FCSTD DOCUMENT  (FreeCAD 1.0R39319 (Git))
Label: Assembly
License: All rights reserved
LicenseURL: https://en.wikipedia.org/wiki/All_rights_reserved
objects: App::Link×10, App::FeaturePython×9, Assembly::JointGroup×1, Assembly::AssemblyObject×1
EXTERNAL_REF file=TopEnclosureShell.FCStd obj=Body002
EXTERNAL_REF file=Spec.FCStd obj=Spreadsheet
EXTERNAL_REF file=TopEnclosureDisplayFront.FCStd obj=Body
EXTERNAL_REF file=TopEnclosureDisplayBack.FCStd obj=Body
EXTERNAL_REF file=TopEnclosureBack_v2.FCStd obj=Body
EXTERNAL_REF file=BottomEnclosure_base_split.FCStd obj=Body002
EXTERNAL_REF file=BottomEnclosure_base_split.FCStd obj=Body003
EXTERNAL_REF file=TopEnclosureHood_v2.FCStd obj=Body
EXTERNAL_REF file=CM5-IO-BASE-B.FCStd obj=PCB

FEATURE [App::Link] Link  label="Top Enclosure Shell - 2"
  LinkPlacement = pos=(-0.4,61.7894,81.5417) rot=(1,0,0;1.0472rad)
  LinkedObject = -> <external TopEnclosureShell.FCStd>#Body002
  Placement = pos=(-0.4,61.7894,81.5417) rot=(1,0,0;1.0472rad)
FEATURE [App::Link] Link002  label="Vars"
  LinkedObject = -> <external Spec.FCStd>#Spreadsheet
FEATURE [App::Link] Top_Enclosure_Display_Front  label="Top Enclosure Display Front"
  LinkPlacement = pos=(-0.4,53.3024,86.4417) rot=(1,0,0;1.0472rad)
  LinkedObject = -> <external TopEnclosureDisplayFront.FCStd>#Body
  Placement = pos=(-0.4,53.3024,86.4417) rot=(1,0,0;1.0472rad)
FEATURE [App::Link] Top_Enclosure_Display_Back  label="Top Enclosure Display Back"
  LinkPlacement = pos=(-0.4,54.6014,85.6917) rot=(0,-0.5,0.866025;3.14159rad)
  LinkedObject = -> <external TopEnclosureDisplayBack.FCStd>#Body
  Placement = pos=(-0.4,54.6014,85.6917) rot=(0,-0.5,0.866025;3.14159rad)
FEATURE [App::Link] Top_Enclosure_Back  label="Top Enclosure Back"
  LinkPlacement = pos=(-0.4,59.4512,82.8917) rot=(0,0.866025,0.5;3.14159rad)
  LinkedObject = -> <external TopEnclosureBack_v2.FCStd>#Body
  Placement = pos=(-0.4,59.4512,82.8917) rot=(0,0.866025,0.5;3.14159rad)
FEATURE [App::Link] Bottom_Enclosure___Bottom  label="Bottom Enclosure - Bottom"
  LinkedObject = -> <external BottomEnclosure_base_split.FCStd>#Body002
FEATURE [App::FeaturePython] GroundedJoint001  # Assembly grounded joint (typed FeaturePython)
  ObjectToGround = -> Bottom_Enclosure___Bottom
FEATURE [App::Link] Bottom_Enclosure___Top  label="Bottom Enclosure - Top"
  LinkPlacement = pos=(1.05e-14,-1.7e-15,5e-16) rot=(0,0,1;0rad)
  LinkedObject = -> <external BottomEnclosure_base_split.FCStd>#Body003
  Placement = pos=(1.05e-14,-1.7e-15,5e-16) rot=(0,0,1;0rad)
FEATURE [App::Link] Top_Enclosure_Hood  label="Top Enclosure Hood"
  LinkPlacement = pos=(-0.4,50.0115,88.3417) rot=(1,0,0;1.0472rad)
  LinkedObject = -> <external TopEnclosureHood_v2.FCStd>#Body
  Placement = pos=(-0.4,50.0115,88.3417) rot=(1,0,0;1.0472rad)
FEATURE [App::Link] PCB
  LinkPlacement = pos=(-110,162,8.00005) rot=(0,0,1;0rad)
  LinkedObject = -> <external CM5-IO-BASE-B.FCStd>#PCB
  Placement = pos=(-110,162,8.00005) rot=(0,0,1;0rad)
FEATURE [App::FeaturePython] Joint  label="Fixed"  # Assembly joint (typed FeaturePython)
  Activated = true
  AngleMax = 0
  AngleMin = 0
  Detach1 = false
  Detach2 = false
  Distance = 0
  Distance2 = 0
  EnableAngleMax = false
  EnableAngleMin = false
  EnableLengthMax = false
  EnableLengthMin = false
  JointType = 0 (Fixed)
  LengthMax = 0
  LengthMin = 0
  Placement1 = pos=(-130,50,15) rot=(1,0,0;3.14159rad)
  Placement2 = pos=(-130,50,15) rot=(1,0,0;3.14159rad)
  Reference1 = -> Assembly [Bottom_Enclosure___Bottom.Edge52,Bottom_Enclosure___Bottom.Edge52]
  Reference2 = -> Assembly [Bottom_Enclosure___Top.Edge108,Bottom_Enclosure___Top.Edge108]
FEATURE [App::FeaturePython] Joint001  label="Cylindrical"  # Assembly joint (typed FeaturePython)
  Activated = true
  AngleMax = 60
  AngleMin = 40
  Detach1 = false
  Detach2 = false
  Distance = 0
  Distance2 = 0
  EnableAngleMax = true
  EnableAngleMin = true
  EnableLengthMax = false
  EnableLengthMin = false
  JointType = 2 (Cylindrical)
  LengthMax = 0
  LengthMin = 0
  Placement1 = pos=(-110.4,15,33.5) rot=(0.57735,0.57735,0.57735;2.0944rad)
  Placement2 = pos=(-108,-65,16.5) rot=(0.57735,0.57735,0.57735;2.0944rad)
  Reference1 = -> Assembly [Bottom_Enclosure___Top.Edge146,Bottom_Enclosure___Top.Edge146]
  Reference2 = -> Assembly [Link.Edge118,Link.Edge118]
FEATURE [App::FeaturePython] Joint002  label="Angle"  # Assembly joint (typed FeaturePython)
  Activated = true
  AngleMax = 0
  AngleMin = 0
  Detach1 = false
  Detach2 = false
  Distance = 0
  Distance2 = 0
  EnableAngleMax = false
  EnableAngleMin = false
  EnableLengthMax = false
  EnableLengthMin = false
  JointType = 8 (Angle)
  LengthMax = 0
  LengthMin = 0
  Placement1 = pos=(117.9,31.739,38.8469) rot=(-0.250563,0.250563,0.935113;1.63783rad)
  Placement2 = pos=(130,-50,-7.1e-15) rot=(-1,0,0;1.5708rad)
  Reference1 = -> Assembly [Bottom_Enclosure___Top.Face63,Bottom_Enclosure___Top.Face63]
  Reference2 = -> Assembly [Link.Face9,Link.Vertex11]
FEATURE [App::FeaturePython] Joint003  label="Distance"  # Assembly joint (typed FeaturePython)
  Activated = true
  AngleMax = 0
  AngleMin = 0
  Detach1 = false
  Detach2 = false
  Distance = 2
  Distance2 = 0
  EnableAngleMax = false
  EnableAngleMin = false
  EnableLengthMax = false
  EnableLengthMin = false
  JointType = 5 (Distance)
  LengthMax = 0
  LengthMin = 0
  Placement1 = pos=(-110.4,18.0202,35.0622) rot=(0.707107,0,0.707107;3.14159rad)
  Placement2 = pos=(-108,-61.4842,13.687) rot=(0.707107,0,0.707107;3.14159rad)
  Reference1 = -> Assembly [Bottom_Enclosure___Top.Face27,Bottom_Enclosure___Top.Face27]
  Reference2 = -> Assembly [Link.Face26,Link.Face26]
FEATURE [App::FeaturePython] Joint004  label="Fixed001"  # Assembly joint (typed FeaturePython)
  Activated = true
  AngleMax = 0
  AngleMin = 0
  Detach1 = false
  Detach2 = false
  Distance = 0
  Distance2 = 0
  EnableAngleMax = false
  EnableAngleMin = false
  EnableLengthMax = false
  EnableLengthMin = false
  JointType = 0 (Fixed)
  LengthMax = 0
  LengthMin = 0
  Offset2 = pos=(0,0,0) rot=(0,0,1;3.14159rad)
  Placement1 = pos=(0,42.4,8.3) rot=(0,0,1;3.14159rad)
  Placement2 = pos=(0,-42.4,-2.84e-14) rot=(0,0,1;0rad)
  Reference1 = -> Assembly [Link.Edge160,Link.Edge160]
  Reference2 = -> Assembly [Top_Enclosure_Display_Back.Edge23,Top_Enclosure_Display_Back.Edge23]
FEATURE [App::FeaturePython] Joint005  label="Fixed002"  # Assembly joint (typed FeaturePython)
  Activated = true
  AngleMax = 0
  AngleMin = 0
  Detach1 = false
  Detach2 = false
  Distance = 0
  Distance2 = 0
  EnableAngleMax = false
  EnableAngleMin = false
  EnableLengthMax = false
  EnableLengthMin = false
  JointType = 0 (Fixed)
  LengthMax = 0
  LengthMin = 0
  Offset2 = pos=(0,0,0) rot=(0,0,1;3.14159rad)
  Placement1 = pos=(0,-42.4,1.5) rot=(0,0,-1;3.14159rad)
  Placement2 = pos=(0,42.4,1.42e-14) rot=(1,0,0;3.14159rad)
  Reference1 = -> Assembly [Top_Enclosure_Display_Back.Edge75,Top_Enclosure_Display_Back.Edge75]
  Reference2 = -> Assembly [Top_Enclosure_Display_Front.Edge64,Top_Enclosure_Display_Front.Edge64]
FEATURE [App::FeaturePython] Joint006  label="Fixed003"  # Assembly joint (typed FeaturePython)
  Activated = true
  AngleMax = 0
  AngleMin = 0
  Detach1 = false
  Detach2 = false
  Distance = 0
  Distance2 = 0
  EnableAngleMax = false
  EnableAngleMin = false
  EnableLengthMax = false
  EnableLengthMin = false
  JointType = 0 (Fixed)
  LengthMax = 0
  LengthMin = 0
  Placement1 = pos=(0,42.4,6.5) rot=(0,0,1;3.14159rad)
  Placement2 = pos=(0,42.4,2.7) rot=(0,0,1;3.14159rad)
  Reference1 = -> Assembly [Top_Enclosure_Display_Front.Edge21,Top_Enclosure_Display_Front.Edge21]
  Reference2 = -> Assembly [Top_Enclosure_Hood.Edge85,Top_Enclosure_Hood.Edge85]
FEATURE [App::FeaturePython] Joint007  label="Fixed004"  # Assembly joint (typed FeaturePython)
  Activated = true
  AngleMax = 0
  AngleMin = 0
  Detach1 = false
  Detach2 = false
  Distance = 0
  Distance2 = 0
  EnableAngleMax = false
  EnableAngleMin = false
  EnableLengthMax = false
  EnableLengthMin = false
  JointType = 0 (Fixed)
  LengthMax = 0
  LengthMin = 0
  Offset2 = pos=(0,0,0) rot=(0,0,1;3.14159rad)
  Placement1 = pos=(0,42.4,2.7) rot=(0,0,1;3.14159rad)
  Placement2 = pos=(0,42.4,0) rot=(-1,0,0;3.14159rad)
  Reference1 = -> Assembly [Link.Edge158,Link.Edge158]
  Reference2 = -> Assembly [Top_Enclosure_Back.Edge28,Top_Enclosure_Back.Edge28]
FEATURE [Assembly::JointGroup] Joints
  Group = -> [GroundedJoint001,Joint,Joint001,Joint002,Joint003,Joint004,Joint005,Joint006,Joint007]
FEATURE [Assembly::AssemblyObject] Assembly
  Group = -> [Joints,Link,Top_Enclosure_Display_Front,Top_Enclosure_Display_Back,Top_Enclosure_Back,Bottom_Enclosure___Bottom,Bottom_Enclosure___Top,GroundedJoint001,Top_Enclosure_Hood,PCB,Joint,Joint001,Joint002,Joint003,Joint004,Joint005,Joint006,Joint007]
  Origin = -> Origin
  Type = Assembly
FEATURE [App::Link] Link003  label="Vars001"
  LinkedObject = -> <external Spec.FCStd>#Spreadsheet

RESOLVED EXTERNAL PARTS (link-assembly join: the EXTERNAL_REF files above that resolve inside this repo's crawl, each included once):
---- part BottomEnclosure_base_split.FCStd = doc fcstd_8ac0cee592a7 ----
FCSTD DOCUMENT  (FreeCAD 1.0R39319 (Git))
Label: BottomEnclosure_base_split
License: All rights reserved
LicenseURL: https://en.wikipedia.org/wiki/All_rights_reserved
objects: PartDesign::Body×4, Sketcher::SketchObject×3, PartDesign::SubShapeBinder×3, PartDesign::Boolean×3, Part::FeaturePython×3, App::VarSet×1, App::Link×1, Part::Extrusion×1, App::DocumentObjectGroup×1, PartDesign::Pad×1, PartDesign::Chamfer×1, PartDesign::Pocket×1
note: 32 computed .brp shape members not serialized (recipe doc carries the construction recipe); baked Part::Feature solids carry a one-line shape summary decoded from their .brp
EXTERNAL_REF file=BottomEnclosure_base.FCStd obj=Body

FEATURE [App::VarSet] VarSet  label="LocalVars"
  BoltLength = 12
  SplitHeight = 15
FEATURE [Sketcher::SketchObject] Sketch
  ArcFitTolerance = 1e-06
  AttachmentSupport = -> [YZ_Plane]
  FullyConstrained = true
  MakeInternals = false
  MapMode = 5
  Placement = pos=(0,0,0) rot=(0.57735,0.57735,0.57735;2.0944rad)
  expr: Constraints[1] = <<LocalVars>>.SplitHeight
  sketch-geometry (1):
    g0: LineSegment StartX=-150 StartY=15 StartZ=0 EndX=150 EndY=15 EndZ=0
  constraints (3):
    c: Symmetric(g0,g0,g-2)
    c: DistanceY(g-1,g0) = 15
    c: DistanceX(g0,g0) = 300
FEATURE [PartDesign::Body] Body  label="Bottom Enclosure Split Line"
  AllowCompound = false
  Group = -> [Sketch]
  Origin = -> Origin
FEATURE [App::Link] Link  label="Bottom Enclosure - AIR40"
  LinkedObject = -> <external BottomEnclosure_base.FCStd>#Body
FEATURE [PartDesign::SubShapeBinder] Binder
  BindCopyOnChange = 0
  BindMode = 0
  ClaimChildren = false
  Context = -> Body001 [Binder.]
  Fuse = false
  MakeFace = true
  OffsetFill = false
  OffsetIntersection = false
  OffsetJoinType = 0
  OffsetOpenResult = false
  PartialLoad = false
  Refine = true
  Relative = true
  Support = -> [Link]
  _Version = 2
FEATURE [PartDesign::Boolean] Boolean
  Group = -> [Binder]
  Refine = true
  Suppressed = false
  Type = 0
  UsePlacement = true
FEATURE [PartDesign::Body] Body001  label="Bottom Enclosure Split Object"
  AllowCompound = false
  Group = -> [Boolean]
  Origin = -> Origin001
  Tip = -> Boolean
FEATURE [Part::Extrusion] Extrude
  Base = -> Sketch
  Dir = (1,0,0)
  DirMode = 2
  FaceMakerClass = Part::FaceMakerBullseye
  FaceMakerMode = 3
  LengthFwd = 500
  LengthRev = 0
  Solid = false
  Symmetric = true
FEATURE [Part::FeaturePython] Slice  # WARN: FeaturePython — macro-defined, semantics opaque (R4)
  Base = -> Body001
  Mode = 1
  Tolerance = 0
  Tools = -> [Extrude]
FEATURE [Part::FeaturePython] Slice_child0  label="Slice.0"  # WARN: FeaturePython — macro-defined, semantics opaque (R4)
  Base = -> Slice
  FilterType = 1
  Invert = false
  OverrideMaxVal = 0
  WindowFrom = 80
  WindowTo = 100
  items = 0
FEATURE [Part::FeaturePython] Slice_child1  label="Slice.1"  # WARN: FeaturePython — macro-defined, semantics opaque (R4)
  Base = -> Slice
  FilterType = 1
  Invert = false
  OverrideMaxVal = 0
  WindowFrom = 80
  WindowTo = 100
  items = 1
FEATURE [App::DocumentObjectGroup] GrExplode_Slice  label="Exploded Slice"
  Group = -> [Slice_child0,Slice_child1]
FEATURE [PartDesign::SubShapeBinder] Binder001
  BindCopyOnChange = 0
  BindMode = 0
  ClaimChildren = false
  Context = -> Body002 [Boolean001.Binder001.]
  Fuse = false
  MakeFace = true
  OffsetFill = false
  OffsetIntersection = false
  OffsetJoinType = 0
  OffsetOpenResult = false
  PartialLoad = false
  Refine = true
  Relative = true
  Support = -> [Slice_child1]
  _Version = 2
FEATURE [PartDesign::SubShapeBinder] Binder002
  BindCopyOnChange = 0
  BindMode = 0
  ClaimChildren = false
  Context = -> Body003 [Boolean002.Binder002.]
  Fuse = false
  MakeFace = true
  OffsetFill = false
  OffsetIntersection = false
  OffsetJoinType = 0
  OffsetOpenResult = false
  PartialLoad = false
  Refine = true
  Relative = true
  Support = -> [Slice_child0]
  _Version = 2
FEATURE [PartDesign::Boolean] Boolean001
  Group = -> [Binder001]
  Refine = true
  Suppressed = false
  Type = 0
  UsePlacement = true
FEATURE [PartDesign::Boolean] Boolean002
  Group = -> [Binder002]
  Refine = true
  Suppressed = false
  Type = 0
  UsePlacement = true
FEATURE [Sketcher::SketchObject] Sketch001
  ArcFitTolerance = 1e-06
  AttachmentSupport = -> [Boolean001]
  ExternalGeometry = -> [Boolean001]
  FullyConstrained = true
  MakeInternals = false
  MapMode = 5
  Placement = pos=(0,0,15) rot=(0,0,1;0rad)
  sketch-geometry (8):
    g0: ArcOfCircle CenterX=-130 CenterY=35 CenterZ=0 NormalX=0 NormalY=0 NormalZ=1 AngleXU=0 Radius=2 StartAngle=2.1969e-12 EndAngle=3.14159
    g1: ArcOfCircle CenterX=-130 CenterY=-75 CenterZ=0 NormalX=0 NormalY=0 NormalZ=1 AngleXU=0 Radius=2 StartAngle=3.14159 EndAngle=6.28319
    g2: LineSegment StartX=-128 StartY=35 StartZ=0 EndX=-128 EndY=-75 EndZ=0
    g3: LineSegment StartX=-132 StartY=35 StartZ=0 EndX=-132 EndY=-75 EndZ=0
    g4: ArcOfCircle CenterX=130 CenterY=35 CenterZ=0 NormalX=0 NormalY=0 NormalZ=1 AngleXU=0 Radius=2 StartAngle=2.1977e-12 EndAngle=3.14159
    g5: ArcOfCircle CenterX=130 CenterY=-75 CenterZ=0 NormalX=0 NormalY=0 NormalZ=1 AngleXU=0 Radius=2 StartAngle=3.14159 EndAngle=6.28319
    g6: LineSegment StartX=132 StartY=35 StartZ=0 EndX=132 EndY=-75 EndZ=0
    g7: LineSegment StartX=128 StartY=35 StartZ=0 EndX=128 EndY=-75 EndZ=0
  constraints (20):
    c: Tangent(g0,g2) = 1.5708
    c: Tangent(g0,g3) = -1.5708
    c: Tangent(g1,g2) = 1.5708
    c: Tangent(g1,g3) = -1.5708
    c: Equal(g0,g1)
    c: Radius(g0) = 2
    c: Vertical(g2)
    c: Tangent(g4,g6) = 1.5708
    c: Tangent(g4,g7) = -1.5708
    c: Tangent(g5,g6) = 1.5708
    c: Tangent(g5,g7) = -1.5708
    c: Equal(g4,g5)
    c: Radius(g4) = 2
    c: Vertical(g6)
    c: Vertical(g-3,g0)
    c: Vertical(g-6,g4)
    c: Horizontal(g4,g0)
    c: Horizontal(g1,g5)
    c: DistanceY(g0,g-3) = 15
    c: DistanceY(g-4,g1) = 15
FEATURE [PartDesign::Pad] Pad
  BaseFeature = -> Boolean001
  Direction = (0,0,1)
  Length = 2
  Length2 = 10
  Profile = -> Sketch001
  ReferenceAxis = -> Sketch001 [N_Axis]
  Refine = true
  Suppressed = false
  Type = 0
FEATURE [PartDesign::Chamfer] Chamfer
  Angle = 45
  Base = -> Pad [Edge136,Edge148]
  BaseFeature = -> Pad
  ChamferType = 0
  FlipDirection = false
  Refine = true
  Size = 0.5
  Size2 = 1
  SupportTransform = false
  Suppressed = false
  UseAllEdges = false
FEATURE [PartDesign::Body] Body002  label="Bottom Enclosure - Bottom"
  AllowCompound = false
  Group = -> [Boolean001,Sketch001,Pad,Chamfer]
  Origin = -> Origin002
  Tip = -> Chamfer
FEATURE [Sketcher::SketchObject] Sketch002
  ArcFitTolerance = 1e-06
  AttachmentSupport = -> [Boolean002]
  ExternalGeometry = -> [Boolean002]
  FullyConstrained = true
  MakeInternals = false
  MapMode = 5
  Placement = pos=(0,0,15) rot=(1,0,0;3.14159rad)
  sketch-geometry (8):
    g0: ArcOfCircle CenterX=-130 CenterY=75 CenterZ=0 NormalX=0 NormalY=0 NormalZ=1 AngleXU=0 Radius=2.2 StartAngle=-2.7e-15 EndAngle=3.14159
    g1: ArcOfCircle CenterX=-130 CenterY=-35 CenterZ=0 NormalX=0 NormalY=0 NormalZ=1 AngleXU=0 Radius=2.2 StartAngle=3.14159 EndAngle=6.28319
    g2: LineSegment StartX=-127.8 StartY=75 StartZ=0 EndX=-127.8 EndY=-35 EndZ=0
    g3: LineSegment StartX=-132.2 StartY=75 StartZ=0 EndX=-132.2 EndY=-35 EndZ=0
    g4: ArcOfCircle CenterX=130 CenterY=75 CenterZ=0 NormalX=0 NormalY=0 NormalZ=1 AngleXU=0 Radius=2.5 StartAngle=7e-16 EndAngle=3.14159
    g5: ArcOfCircle CenterX=130 CenterY=-35 CenterZ=0 NormalX=0 NormalY=0 NormalZ=1 AngleXU=0 Radius=2.5 StartAngle=3.14159 EndAngle=6.28319
    g6: LineSegment StartX=132.5 StartY=75 StartZ=0 EndX=132.5 EndY=-35 EndZ=0
    g7: LineSegment StartX=127.5 StartY=75 StartZ=0 EndX=127.5 EndY=-35 EndZ=0
  constraints (20):
    c: Tangent(g0,g2) = 1.5708
    c: Tangent(g0,g3) = -1.5708
    c: Tangent(g1,g2) = 1.5708
    c: Tangent(g1,g3) = -1.5708
    c: Equal(g0,g1)
    c: Vertical(g3)
    c: Radius(g0) = 2.2
    c: Tangent(g4,g6) = 1.5708
    c: Tangent(g4,g7) = -1.5708
    c: Tangent(g5,g6) = 1.5708
    c: Tangent(g5,g7) = -1.5708
    c: Equal(g4,g5)
    c: Radius(g4) = 2.5
    c: Vertical(g6)
    c: Vertical(g4,g-6)
    c: Horizontal(g4,g0)
    c: Vertical(g0,g-3)
    c: Horizontal(g1,g5)
    c: DistanceY(g0,g-3) = 15
    c: DistanceY(g-4,g1) = 15
FEATURE [PartDesign::Pocket] Pocket
  BaseFeature = -> Boolean002
  Direction = (0,0,1)
  Length = 3
  Length2 = 5
  Profile = -> Sketch002
  ReferenceAxis = -> Sketch002 [N_Axis]
  Refine = true
  Suppressed = false
  Type = 0
FEATURE [PartDesign::Body] Body003  label="Bottom Enclosure - Top"
  AllowCompound = false
  Group = -> [Boolean002,Sketch002,Pocket]
  Origin = -> Origin003
  Tip = -> Pocket
---- part Spec.FCStd = doc fcstd_a8ec68f4a39c ----
FCSTD DOCUMENT  (FreeCAD 1.0R39319 (Git))
Label: Spec
License: All rights reserved
LicenseURL: https://en.wikipedia.org/wiki/All_rights_reserved
objects: Spreadsheet::Sheet×1

FEATURE [Spreadsheet::Sheet] Spreadsheet  label="Vars"
  cells = A1='Common; A2='clearance; B2(clearance)=0.2; A3='nut_inserts_m2; B3(nut_inserts_m2)=3.5; A4='nut_inserts_m3; B4(nut_inserts_m3)=4.5; A5='wall; B5(wall)=2.5; A6='ext_radius; B6(ext_radius)=10; A7='hood_angle; B7(hood_angle)=4; A12='Display; A13='display_width; B13(display_width)=231.3; A14='display_height; B14(display_height)=64.3; A15='display_depth; B15(display_depth)=5.5; A16='display_offset_bottom; B16(display_offset_bottom)==3 + display_view_offset; C16='display_view_offset; D16(display_view_offset)=1; A17='display_offset_left; B17(display_offset_left)==2.5 + display_view_offset; A18='display_offset_right; B18(display_offset_right)==7.5 + display_view_offset; A19='display_offset_top; B19(display_offset_top)==3 + display_view_offset; F20='b; A21='Top Enclosure; A22='top_enclosure_width; B22(top_enclosure_width)=280; A23='top_enclosure_height; B23(top_enclosure_height)=100; A24='top_enclosure_front_depth; B24(top_enclosure_front_depth)=1; A25='top_enclosure_back_depth; B25(top_enclosure_back_depth)==wall; A26='top_enclosure_display_back_depth; B26(top_enclosure_display_back_depth)=1; A27='top_enclosure_depth; B27(top_enclosure_depth)=14; A28='top_enclosure_internal_depth; B28(top_enclosure_internal_depth)==top_enclosure_depth - top_enclosure_front_depth - display_depth - top_enclosure_display_back_depth - top_enclosure_back_depth + wall; A30='Bottom Enclosure; A31='bottom_enclosure_width; B31(bottom_enclosure_width)==top_enclosure_width; A32='bottom_enclosure_height; B32(bottom_enclosure_height)=160; A33='bottom_enclosure_depth; B33(bottom_enclosure_depth)=30; A35='Keyboard Plate; A36='keyboard_plate_width; B36(keyboard_plate_width)==235 - 2; A37='keyboard_plate_height; B37(keyboard_plate_height)==82.5 - 2; A38='keyboard_plate_radius; B38(kayboard_plate_radius)==ext_radius / 2; A40='Keyboard Plate; A41='wire_hole_offset_x; B41(wire_hole_offset_x)=40; A42='wire_hole_width; B42(wire_hole_width)=30; A43='wire_hole_height; B43(wire_hole_height)=9
---- part TopEnclosureBack_v2.FCStd = doc fcstd_1d1bf80cae44 ----
FCSTD DOCUMENT  (FreeCAD 1.0R39319 (Git))
Label: TopEnclosureBack_v2
License: All rights reserved
LicenseURL: https://en.wikipedia.org/wiki/All_rights_reserved
objects: PartDesign::SubShapeBinder×4, Sketcher::SketchObject×3, PartDesign::Pocket×3, PartDesign::Mirrored×3, App::Link×2, PartDesign::Pad×2, PartDesign::Hole×2, PartDesign::MultiTransform×1, PartDesign::Body×1, App::VarSet×1
note: 40 computed .brp shape members not serialized (recipe doc carries the construction recipe); baked Part::Feature solids carry a one-line shape summary decoded from their .brp
EXTERNAL_REF file=TopEnclosure.FCStd obj=Sketch
EXTERNAL_REF file=TopEnclosure.FCStd obj=Link

FEATURE [App::Link] Link  label="MasterSketch"
  LinkedObject = -> <external TopEnclosure.FCStd>#Sketch
FEATURE [App::Link] Link001  label="Vars"
  LinkedObject = -> <external TopEnclosure.FCStd>#Link
FEATURE [PartDesign::SubShapeBinder] Binder
  BindCopyOnChange = 0
  BindMode = 0
  ClaimChildren = false
  Context = -> Body [Binder.]
  Fuse = false
  MakeFace = true
  OffsetFill = false
  OffsetIntersection = false
  OffsetJoinType = 0
  OffsetOpenResult = false
  PartialLoad = false
  Refine = true
  Relative = true
  Support = -> [Link[Edge13,Edge14,Edge15,Edge12,Edge11,Edge10,Edge9,Edge16]]
  _Version = 2
FEATURE [PartDesign::SubShapeBinder] Binder001
  BindCopyOnChange = 0
  BindMode = 0
  ClaimChildren = false
  Context = -> Body [Binder001.]
  Fuse = false
  MakeFace = true
  OffsetFill = false
  OffsetIntersection = false
  OffsetJoinType = 0
  OffsetOpenResult = false
  PartialLoad = false
  Placement = pos=(0,0,2.3) rot=(0,0,1;0rad)
  Refine = true
  Relative = true
  Support = -> [Link[Edge18,Edge17,Edge24,Edge23,Edge19,Edge22,Edge21,Edge20]]
  _Version = 2
  expr: .Placement.Base.z = <<LocalVars>>.bottom_offset
FEATURE [PartDesign::SubShapeBinder] Binder002
  BindCopyOnChange = 0
  BindMode = 0
  ClaimChildren = false
  Context = -> Body [Binder002.]
  Fuse = false
  MakeFace = true
  OffsetFill = false
  OffsetIntersection = false
  OffsetJoinType = 0
  OffsetOpenResult = false
  PartialLoad = false
  Refine = true
  Relative = true
  Support = -> [Link[Edge39]]
  _Version = 2
FEATURE [PartDesign::SubShapeBinder] Binder003
  BindCopyOnChange = 0
  BindMode = 0
  ClaimChildren = false
  Context = -> Body [Binder003.]
  Fuse = false
  MakeFace = true
  OffsetFill = false
  OffsetIntersection = false
  OffsetJoinType = 0
  OffsetOpenResult = false
  PartialLoad = false
  Refine = true
  Relative = true
  Support = -> [Link[Edge40]]
  _Version = 2
FEATURE [PartDesign::Pad] Pad
  Direction = (0,0,1)
  Length = 2.3
  Length2 = 10
  Profile = -> Binder
  Refine = true
  Suppressed = false
  Type = 0
  expr: Length = <<LocalVars>>.bottom_offset
FEATURE [PartDesign::Pad] Pad001
  BaseFeature = -> Pad
  Direction = (0,0,1)
  Length = 1
  Length2 = 10
  Profile = -> Binder001
  Refine = true
  Suppressed = false
  Type = 0
FEATURE [PartDesign::Hole] Hole
  BaseFeature = -> Pad001
  CustomThreadClearance = 0
  Depth = 600.733
  DepthType = 1
  Diameter = 3.6
  DrillForDepth = false
  DrillPoint = 1
  DrillPointAngle = 118
  HoleCutCountersinkAngle = 90
  HoleCutCustomValues = false
  HoleCutDepth = 0
  HoleCutDiameter = 6.1
  HoleCutType = 0
  ModelThread = false
  Profile = -> Binder002
  Refine = true
  Reversed = true
  Suppressed = false
  Tapered = false
  TaperedAngle = 90
  ThreadClass = 0
  ThreadDepth = 600.733
  ThreadDepthType = 0
  ThreadDirection = 0
  ThreadFit = 2
  ThreadSize = 9
  ThreadType = 1
  Threaded = false
  UseCustomThreadClearance = false
FEATURE [Sketcher::SketchObject] Sketch
  ArcFitTolerance = 1e-06
  AttachmentSupport = -> [Hole]
  ExternalGeometry = -> [Hole]
  FullyConstrained = true
  MakeInternals = false
  MapMode = 5
  Placement = pos=(0,0,3.3) rot=(0,0,1;0rad)
  expr: Constraints[19] = <<LocalVars>>.m3_nut_dia
  sketch-geometry (7):
    g0: LineSegment StartX=-129.1 StartY=42.4 StartZ=0 EndX=-130.75 EndY=45.2579 EndZ=0
    g1: LineSegment StartX=-130.75 StartY=45.2579 StartZ=0 EndX=-134.05 EndY=45.2579 EndZ=0
    g2: LineSegment StartX=-134.05 StartY=45.2579 StartZ=0 EndX=-135.7 EndY=42.4 EndZ=0
    g3: LineSegment StartX=-135.7 StartY=42.4 StartZ=0 EndX=-134.05 EndY=39.5421 EndZ=0
    g4: LineSegment StartX=-134.05 StartY=39.5421 StartZ=0 EndX=-130.75 EndY=39.5421 EndZ=0
    g5: LineSegment StartX=-130.75 StartY=39.5421 StartZ=0 EndX=-129.1 EndY=42.4 EndZ=0
    g6: Circle [constr] CenterX=-132.4 CenterY=42.4 CenterZ=0 NormalX=0 NormalY=0 NormalZ=1 AngleXU=0 Radius=3.3
  constraints (16):
    c: Coincident(g0,g1)
    c: Coincident(g1,g2)
    c: Coincident(g2,g3)
    c: Coincident(g3,g4)
    c: Coincident(g4,g5)
    c: Coincident(g5,g0)
    c: Equal(g0, g1-g5) x5
    c: PointOnObject(g0,g6)
    c: PointOnObject(g1,g6)
    c: PointOnObject(g2,g6)
    c: PointOnObject(g3,g6)
    c: PointOnObject(g4,g6)
    c: PointOnObject(g5,g6)
    c: Coincident(g6,g-3)
    c: Horizontal(g1)
    c: Diameter(g6) = 6.6
FEATURE [PartDesign::Pocket] Pocket
  BaseFeature = -> Hole
  Direction = (0,0,-1)
  Length = 3
  Length2 = 5
  Profile = -> Sketch
  ReferenceAxis = -> Sketch [N_Axis]
  Refine = true
  Suppressed = false
  Type = 0
FEATURE [PartDesign::Mirrored] Mirrored
  MirrorPlane = -> YZ_Plane
  Refine = true
  Suppressed = false
  TransformMode = 0
FEATURE [PartDesign::Mirrored] Mirrored001
  MirrorPlane = -> XZ_Plane
  Refine = true
  Suppressed = false
  TransformMode = 0
FEATURE [PartDesign::MultiTransform] MultiTransform
  BaseFeature = -> Pocket
  Originals = -> [Hole,Pocket]
  Refine = true
  Suppressed = false
  TransformMode = 0
  Transformations = -> [Mirrored,Mirrored001]
FEATURE [PartDesign::Hole] Hole001
  BaseFeature = -> MultiTransform
  CustomThreadClearance = 0
  Depth = 600.733
  DepthType = 1
  Diameter = 3.6
  DrillForDepth = false
  DrillPoint = 1
  DrillPointAngle = 118
  HoleCutCountersinkAngle = 90
  HoleCutCustomValues = false
  HoleCutDepth = 0
  HoleCutDiameter = 6.1
  HoleCutType = 0
  ModelThread = false
  Profile = -> Binder003
  Refine = true
  Reversed = true
  Suppressed = false
  Tapered = false
  TaperedAngle = 90
  ThreadClass = 0
  ThreadDepth = 600.733
  ThreadDepthType = 0
  ThreadDirection = 0
  ThreadFit = 2
  ThreadSize = 9
  ThreadType = 1
  Threaded = false
  UseCustomThreadClearance = false
FEATURE [Sketcher::SketchObject] Sketch001
  ArcFitTolerance = 1e-06
  AttachmentSupport = -> [Hole001]
  ExternalGeometry = -> [Hole001]
  FullyConstrained = true
  MakeInternals = false
  MapMode = 5
  Placement = pos=(0,0,3.3) rot=(0,0,1;0rad)
  expr: Constraints[19] = <<LocalVars>>.m3_nut_dia
  sketch-geometry (7):
    g0: LineSegment StartX=3.3 StartY=42.4 StartZ=0 EndX=1.65 EndY=45.2579 EndZ=0
    g1: LineSegment StartX=1.65 StartY=45.2579 StartZ=0 EndX=-1.65 EndY=45.2579 EndZ=0
    g2: LineSegment StartX=-1.65 StartY=45.2579 StartZ=0 EndX=-3.3 EndY=42.4 EndZ=0
    g3: LineSegment StartX=-3.3 StartY=42.4 StartZ=0 EndX=-1.65 EndY=39.5421 EndZ=0
    g4: LineSegment StartX=-1.65 StartY=39.5421 StartZ=0 EndX=1.65 EndY=39.5421 EndZ=0
    g5: LineSegment StartX=1.65 StartY=39.5421 StartZ=0 EndX=3.3 EndY=42.4 EndZ=0
    g6: Circle [constr] CenterX=0 CenterY=42.4 CenterZ=0 NormalX=0 NormalY=0 NormalZ=1 AngleXU=0 Radius=3.3
  constraints (16):
    c: Coincident(g0,g1)
    c: Coincident(g1,g2)
    c: Coincident(g2,g3)
    c: Coincident(g3,g4)
    c: Coincident(g4,g5)
    c: Coincident(g5,g0)
    c: Equal(g0, g1-g5) x5
    c: PointOnObject(g0,g6)
    c: PointOnObject(g1,g6)
    c: PointOnObject(g2,g6)
    c: PointOnObject(g3,g6)
    c: PointOnObject(g4,g6)
    c: PointOnObject(g5,g6)
    c: Coincident(g6,g-3)
    c: Horizontal(g1)
    c: Diameter(g6) = 6.6
FEATURE [PartDesign::Pocket] Pocket001
  BaseFeature = -> Hole001
  Direction = (0,0,-1)
  Length = 3
  Length2 = 5
  Profile = -> Sketch001
  ReferenceAxis = -> Sketch001 [N_Axis]
  Refine = true
  Suppressed = false
  Type = 0
FEATURE [PartDesign::Mirrored] Mirrored002
  BaseFeature = -> Pocket001
  MirrorPlane = -> XZ_Plane
  Originals = -> [Hole001,Pocket001]
  Refine = true
  Suppressed = false
  TransformMode = 0
FEATURE [Sketcher::SketchObject] Sketch002
  ArcFitTolerance = 1e-06
  AttachmentSupport = -> [XY_Plane]
  ExternalGeometry = -> [Mirrored002]
  FullyConstrained = true
  MakeInternals = false
  MapMode = 5
  sketch-geometry (12):
    g0: LineSegment StartX=127.4 StartY=-32.4 StartZ=0 EndX=127.4 EndY=32.4 EndZ=0
    g1: LineSegment StartX=122.4 StartY=37.4 StartZ=0 EndX=-122.4 EndY=37.4 EndZ=0
    g2: LineSegment StartX=-127.4 StartY=32.4 StartZ=0 EndX=-127.4 EndY=-32.4 EndZ=0
    g3: LineSegment StartX=-122.4 StartY=-37.4 StartZ=0 EndX=122.4 EndY=-37.4 EndZ=0
    g4: ArcOfCircle CenterX=122.4 CenterY=-32.4 CenterZ=0 NormalX=0 NormalY=0 NormalZ=1 AngleXU=0 Radius=5 StartAngle=4.71239 EndAngle=6.28319
    g5: ArcOfCircle CenterX=122.4 CenterY=32.4 CenterZ=0 NormalX=0 NormalY=0 NormalZ=1 AngleXU=0 Radius=5 StartAngle=0 EndAngle=1.5708
    g6: ArcOfCircle CenterX=-122.4 CenterY=32.4 CenterZ=0 NormalX=0 NormalY=0 NormalZ=1 AngleXU=0 Radius=5 StartAngle=1.5708 EndAngle=3.14159
    g7: ArcOfCircle CenterX=-122.4 CenterY=-32.4 CenterZ=0 NormalX=0 NormalY=0 NormalZ=1 AngleXU=0 Radius=5 StartAngle=3.14159 EndAngle=4.71239
    g8: GeomPoint [constr] X=-132.4 Y=42.4 Z=0
    g9: GeomPoint [constr] X=0 Y=0 Z=0
    g10: LineSegment [constr] StartX=0 StartY=47.4 StartZ=0 EndX=0 EndY=37.4 EndZ=0
    g11: LineSegment [constr] StartX=-127.4 StartY=32.4 StartZ=0 EndX=-137.4 EndY=32.4 EndZ=0
  constraints (27):
    c: Tangent(g0,g4) = -1.5708
    c: Tangent(g0,g5) = -1.5708
    c: Tangent(g1,g5) = -1.5708
    c: Tangent(g1,g6) = -1.5708
    c: Tangent(g2,g6) = -1.5708
    c: Tangent(g2,g7) = -1.5708
    c: Tangent(g3,g7) = -1.5708
    c: Tangent(g3,g4) = -1.5708
    c: Vertical(g0)
    c: Vertical(g2)
    c: Horizontal(g1)
    c: Horizontal(g3)
    c: Equal(g4,g5)
    c: Equal(g5,g6)
    c: Equal(g6,g7)
    c: Symmetric(g2,g0,g9)
    c: Coincident(g9,g-1)
    c: Coincident(g8,g-3)
    c: Diameter(g6) = 10
    c: PointOnObject(g10,g-5)
    c: PointOnObject(g10,g1)
    c: Symmetric(g10,g10,g-4)
    c: PointOnObject(g10,g-2)
    c: Coincident(g11,g2)
    c: PointOnObject(g11,g-6)
    c: Horizontal(g11)
    c: Equal(g11,g10)
FEATURE [PartDesign::Pocket] Pocket002
  BaseFeature = -> Mirrored002
  Direction = (0,0,-1)
  Length = 2.5
  Length2 = 5
  Profile = -> Sketch002
  ReferenceAxis = -> Sketch002 [N_Axis]
  Refine = true
  Reversed = true
  Suppressed = false
  Type = 0
FEATURE [PartDesign::Body] Body  label="Top Enclosure Back"
  AllowCompound = false
  Group = -> [Binder,Binder001,Binder002,Binder003,Pad,Pad001,Hole,Sketch,Pocket,MultiTransform,Mirrored,Mirrored001,Hole001,Sketch001,Pocket001,Mirrored002,Sketch002,Pocket002]
  Origin = -> Origin
  Tip = -> Pocket002
FEATURE [App::VarSet] VarSet  label="LocalVars"
  bottom_offset = 2.3
  m3_nut_dia = 6.6
  expr: bottom_offset = <<Vars>>.wall - <<Vars>>.clearance
  expr: m3_nut_dia = 6.2 + 2 * <<Vars>>.clearance
---- part TopEnclosureDisplayBack.FCStd = doc fcstd_2bdf85f48a5a ----
FCSTD DOCUMENT  (FreeCAD 1.0R39319 (Git))
Label: TopEnclosureDisplayBack
License: All rights reserved
LicenseURL: https://en.wikipedia.org/wiki/All_rights_reserved
objects: PartDesign::SubShapeBinder×6, PartDesign::Mirrored×4, PartDesign::Hole×3, Sketcher::SketchObject×3, App::Link×2, PartDesign::Pad×2, PartDesign::MultiTransform×1, PartDesign::Pocket×1, PartDesign::Chamfer×1, PartDesign::Body×1
note: 44 computed .brp shape members not serialized (recipe doc carries the construction recipe); baked Part::Feature solids carry a one-line shape summary decoded from their .brp
EXTERNAL_REF file=Spec.FCStd obj=Spreadsheet
EXTERNAL_REF file=TopEnclosure.FCStd obj=Sketch

FEATURE [App::Link] Link  label="Vars"
  LinkedObject = -> <external Spec.FCStd>#Spreadsheet
FEATURE [App::Link] Link001  label="MasterSketch"
  LinkedObject = -> <external TopEnclosure.FCStd>#Sketch
FEATURE [PartDesign::SubShapeBinder] Binder
  BindCopyOnChange = 0
  BindMode = 0
  ClaimChildren = false
  Context = -> Body [Binder.]
  Fuse = false
  MakeFace = true
  OffsetFill = false
  OffsetIntersection = false
  OffsetJoinType = 0
  OffsetOpenResult = false
  PartialLoad = false
  Refine = true
  Relative = true
  Support = -> [Link001[Edge9,Edge10,Edge11,Edge12,Edge13,Edge14,Edge15,Edge16]]
  _Version = 2
FEATURE [PartDesign::SubShapeBinder] Binder001
  BindCopyOnChange = 0
  BindMode = 0
  ClaimChildren = false
  Context = -> Body [Binder001.]
  Fuse = false
  MakeFace = true
  OffsetFill = false
  OffsetIntersection = false
  OffsetJoinType = 0
  OffsetOpenResult = false
  PartialLoad = false
  Refine = true
  Relative = true
  Support = -> [Link001[Edge39]]
  _Version = 2
FEATURE [PartDesign::SubShapeBinder] Binder002
  BindCopyOnChange = 0
  BindMode = 0
  ClaimChildren = false
  Context = -> Body [Binder002.]
  Fuse = false
  MakeFace = true
  OffsetFill = false
  OffsetIntersection = false
  OffsetJoinType = 0
  OffsetOpenResult = false
  PartialLoad = false
  Refine = true
  Relative = true
  Support = -> [Link001[Edge40]]
  _Version = 2
FEATURE [PartDesign::Pad] Pad
  Direction = (0,0,1)
  Length = 1.5
  Length2 = 10
  Profile = -> Binder
  Refine = true
  Suppressed = false
  Type = 0
  expr: Length = <<Vars>>.top_enclosure_display_back_depth
FEATURE [PartDesign::Hole] Hole
  BaseFeature = -> Pad
  CustomThreadClearance = 0
  Depth = 25
  DepthType = 0
  Diameter = 3.6
  DrillForDepth = false
  DrillPoint = 1
  DrillPointAngle = 118
  HoleCutCountersinkAngle = 90
  HoleCutCustomValues = false
  HoleCutDepth = 0
  HoleCutDiameter = 6.1
  HoleCutType = 0
  ModelThread = false
  Profile = -> Binder001
  Refine = true
  Reversed = true
  Suppressed = false
  Tapered = false
  TaperedAngle = 90
  ThreadClass = 0
  ThreadDepth = 25
  ThreadDepthType = 0
  ThreadDirection = 0
  ThreadFit = 2
  ThreadSize = 9
  ThreadType = 1
  Threaded = false
  UseCustomThreadClearance = false
FEATURE [PartDesign::Mirrored] Mirrored
  MirrorPlane = -> YZ_Plane
  Refine = true
  Suppressed = false
  TransformMode = 0
FEATURE [PartDesign::Mirrored] Mirrored001
  MirrorPlane = -> XZ_Plane
  Refine = true
  Suppressed = false
  TransformMode = 0
FEATURE [PartDesign::MultiTransform] MultiTransform
  BaseFeature = -> Hole
  Originals = -> [Hole]
  Refine = true
  Suppressed = false
  TransformMode = 0
  Transformations = -> [Mirrored,Mirrored001]
FEATURE [PartDesign::Hole] Hole001
  BaseFeature = -> MultiTransform
  CustomThreadClearance = 0
  Depth = 25
  DepthType = 0
  Diameter = 3.6
  DrillForDepth = false
  DrillPoint = 1
  DrillPointAngle = 118
  HoleCutCountersinkAngle = 90
  HoleCutCustomValues = false
  HoleCutDepth = 0
  HoleCutDiameter = 6.1
  HoleCutType = 0
  ModelThread = false
  Profile = -> Binder002
  Refine = true
  Reversed = true
  Suppressed = false
  Tapered = false
  TaperedAngle = 90
  ThreadClass = 0
  ThreadDepth = 25
  ThreadDepthType = 0
  ThreadDirection = 0
  ThreadFit = 2
  ThreadSize = 9
  ThreadType = 1
  Threaded = false
  UseCustomThreadClearance = false
FEATURE [PartDesign::Mirrored] Mirrored002
  BaseFeature = -> Hole001
  MirrorPlane = -> XZ_Plane
  Originals = -> [Hole001]
  Refine = true
  Suppressed = false
  TransformMode = 0
FEATURE [PartDesign::SubShapeBinder] Binder003
  BindCopyOnChange = 0
  BindMode = 0
  ClaimChildren = false
  Context = -> Body [Binder003.]
  Fuse = false
  MakeFace = true
  OffsetFill = false
  OffsetIntersection = false
  OffsetJoinType = 0
  OffsetOpenResult = false
  PartialLoad = false
  Refine = true
  Relative = true
  Support = -> [Link001[Edge47]]
  _Version = 2
FEATURE [PartDesign::SubShapeBinder] Binder004
  BindCopyOnChange = 0
  BindMode = 0
  ClaimChildren = false
  Context = -> Body [Binder004.]
  Fuse = false
  MakeFace = true
  OffsetFill = false
  OffsetIntersection = false
  OffsetJoinType = 0
  OffsetOpenResult = false
  PartialLoad = false
  Refine = true
  Relative = true
  Support = -> [Link001[Edge35]]
  _Version = 2
FEATURE [Sketcher::SketchObject] Sketch001
  ArcFitTolerance = 1e-06
  AttachmentSupport = -> [XY_Plane]
  ExternalGeometry = -> [Binder004]
  FullyConstrained = true
  MakeInternals = false
  MapMode = 5
  sketch-geometry (15):
    g0: LineSegment StartX=88.25 StartY=4.75 StartZ=0 EndX=88.25 EndY=-20.25 EndZ=0
    g1: LineSegment StartX=0.25 StartY=18.25 StartZ=0 EndX=0.25 EndY=-20.25 EndZ=0
    g2: LineSegment StartX=3.25 StartY=-23.25 StartZ=0 EndX=57.25 EndY=-23.25 EndZ=0
    g3: LineSegment StartX=60.25 StartY=-20.25 StartZ=0 EndX=60.25 EndY=18.25 EndZ=0
    g4: LineSegment StartX=57.25 StartY=21.25 StartZ=0 EndX=3.25 EndY=21.25 EndZ=0
    g5: ArcOfCircle CenterX=3.25 CenterY=18.25 CenterZ=0 NormalX=0 NormalY=0 NormalZ=1 AngleXU=0 Radius=3 StartAngle=1.5708 EndAngle=3.14159
    g6: ArcOfCircle CenterX=3.25 CenterY=-20.25 CenterZ=0 NormalX=0 NormalY=0 NormalZ=1 AngleXU=0 Radius=3 StartAngle=3.14159 EndAngle=4.71239
    g7: ArcOfCircle CenterX=57.25 CenterY=-20.25 CenterZ=0 NormalX=0 NormalY=0 NormalZ=1 AngleXU=0 Radius=3 StartAngle=4.71239 EndAngle=6.28319
    g8: ArcOfCircle CenterX=57.25 CenterY=18.25 CenterZ=0 NormalX=0 NormalY=0 NormalZ=1 AngleXU=0 Radius=3 StartAngle=-9e-16 EndAngle=1.5708
    g9: GeomPoint [constr] X=0.25 Y=21.25 Z=0
    g10: GeomPoint [constr] X=60.25 Y=-23.25 Z=0
    g11: LineSegment StartX=58.25 StartY=4.75 StartZ=0 EndX=58.25 EndY=-20.25 EndZ=0
    g12: Circle CenterX=3 CenterY=18.75 CenterZ=0 NormalX=0 NormalY=0 NormalZ=1 AngleXU=0 Radius=1.5
    g13: Circle CenterX=44.25 CenterY=17.65 CenterZ=0 NormalX=0 NormalY=0 NormalZ=1 AngleXU=0 Radius=1.5
    g14: Circle CenterX=17.25 CenterY=-19.65 CenterZ=0 NormalX=0 NormalY=0 NormalZ=1 AngleXU=0 Radius=1.5
  constraints (41):
    c: Vertical(g0)
    c: DistanceX(g0,g-3) = 30
    c: DistanceY(g-3,g0) = 12
    c: DistanceY(g0,g0) = 25
    c: Tangent(g1,g5) = -1.5708
    c: Tangent(g1,g6) = -1.5708
    c: Tangent(g2,g6) = -1.5708
    c: Tangent(g2,g7) = -1.5708
    c: Tangent(g3,g7) = -1.5708
    c: Tangent(g3,g8) = -1.5708
    c: Tangent(g4,g8) = -1.5708
    c: Tangent(g4,g5) = -1.5708
    c: Vertical(g1)
    c: Vertical(g3)
    c: Horizontal(g2)
    c: Horizontal(g4)
    c: Equal(g5,g6)
    c: Equal(g6,g7)
    c: Equal(g7,g8)
    c: PointOnObject(g9,g1)
    c: PointOnObject(g9,g4)
    c: PointOnObject(g10,g2)
    c: PointOnObject(g10,g3)
    c: DistanceX(g1,g3) = 60
    c: DistanceY(g2,g4) = 44.5
    c: Radius(g6) = 3
    c: Distance(g11) = 25
    c: Vertical(g11)
    c: DistanceY(g2,g11) = 3
    c: DistanceX(g11,g3) = 2
    c: Horizontal(g11,g0)
    c: Equal(g14,g13)
    c: Equal(g13,g12)
    c: Diameter(g13) = 3
    c: DistanceY(g12,g4) = 2.5
    c: DistanceX(g1,g12) = 2.75
    c: DistanceY(g2,g14) = 3.6
    c: DistanceX(g1,g14) = 17
    c: DistanceY(g13,g4) = 3.6
    c: DistanceX(g13,g3) = 16
    c: DistanceX(g11,g0) = 30
FEATURE [Sketcher::SketchObject] Sketch
  ArcFitTolerance = 1e-06
  AttachmentSupport = -> [XY_Plane]
  ExternalGeometry = -> [Binder003,Sketch001]
  FullyConstrained = true
  MakeInternals = false
  MapMode = 5
  sketch-geometry (8):
    g0: LineSegment StartX=78.25 StartY=23.25 StartZ=0 EndX=78.25 EndY=-23.25 EndZ=0
    g1: LineSegment StartX=84.25 StartY=-29.25 StartZ=0 EndX=142.4 EndY=-29.25 EndZ=0
    g2: LineSegment StartX=142.4 StartY=-29.25 StartZ=0 EndX=142.4 EndY=29.25 EndZ=0
    g3: LineSegment StartX=142.4 StartY=29.25 StartZ=0 EndX=84.25 EndY=29.25 EndZ=0
    g4: ArcOfCircle CenterX=84.25 CenterY=23.25 CenterZ=0 NormalX=0 NormalY=0 NormalZ=1 AngleXU=0 Radius=6 StartAngle=1.5708 EndAngle=3.14159
    g5: GeomPoint [constr] X=78.25 Y=29.25 Z=0
    g6: ArcOfCircle CenterX=84.25 CenterY=-23.25 CenterZ=0 NormalX=0 NormalY=0 NormalZ=1 AngleXU=0 Radius=6 StartAngle=3.14159 EndAngle=4.71239
    g7: GeomPoint [constr] X=78.25 Y=-29.25 Z=0
  constraints (19):
    c: Coincident(g1,g2)
    c: Coincident(g2,g3)
    c: Vertical(g0)
    c: Horizontal(g1)
    c: Horizontal(g3)
    c: Symmetric(g1,g2,g-1)
    c: DistanceY(g-3,g2) = 2
    c: DistanceX(g-4,g2) = 5
    c: PointOnObject(g5,g0)
    c: PointOnObject(g5,g3)
    c: Tangent(g0,g4) = -1.5708
    c: Tangent(g3,g4) = -1.5708
    c: PointOnObject(g7,g0)
    c: PointOnObject(g7,g1)
    c: Tangent(g0,g6) = -1.5708
    c: Tangent(g1,g6) = -1.5708
    c: Equal(g6,g4)
    c: Equal(g4,g-4)
    c: DistanceX(g0,g-6) = 10
FEATURE [PartDesign::Pocket] Pocket
  BaseFeature = -> Mirrored002
  Direction = (0,0,-1)
  Length = 5
  Length2 = 5
  Profile = -> Sketch
  ReferenceAxis = -> Sketch [N_Axis]
  Refine = true
  Reversed = true
  Suppressed = false
  Type = 1
FEATURE [PartDesign::Mirrored] Mirrored003
  BaseFeature = -> Pocket
  MirrorPlane = -> Sketch [V_Axis]
  Originals = -> [Pocket]
  Refine = true
  Suppressed = false
  TransformMode = 0
FEATURE [Sketcher::SketchObject] Sketch002
  ArcFitTolerance = 1e-06
  AttachmentSupport = -> [XY_Plane]
  ExternalGeometry = -> [Sketch001]
  FullyConstrained = true
  MakeInternals = false
  MapMode = 5
  sketch-geometry (3):
    g0: Circle CenterX=3 CenterY=18.75 CenterZ=0 NormalX=0 NormalY=0 NormalZ=1 AngleXU=0 Radius=3.5
    g1: Circle CenterX=44.25 CenterY=17.65 CenterZ=0 NormalX=0 NormalY=0 NormalZ=1 AngleXU=0 Radius=3.5
    g2: Circle CenterX=17.25 CenterY=-19.65 CenterZ=0 NormalX=0 NormalY=0 NormalZ=1 AngleXU=0 Radius=3.5
  constraints (6):
    c: Coincident(g0,g-4)
    c: Coincident(g1,g-3)
    c: Coincident(g2,g-5)
    c: Equal(g2,g0)
    c: Equal(g0,g1)
    c: Diameter(g0) = 7
FEATURE [PartDesign::Pad] Pad001
  BaseFeature = -> Mirrored003
  Direction = (0,0,1)
  Length = 2.5
  Length2 = 10
  Profile = -> Sketch002
  ReferenceAxis = -> Sketch002 [N_Axis]
  Refine = true
  Reversed = true
  Suppressed = false
  Type = 0
FEATURE [PartDesign::SubShapeBinder] Binder005
  BindCopyOnChange = 0
  BindMode = 0
  ClaimChildren = false
  Context = -> Body [Binder005.]
  Fuse = false
  MakeFace = true
  OffsetFill = false
  OffsetIntersection = false
  OffsetJoinType = 0
  OffsetOpenResult = false
  PartialLoad = false
  Placement = pos=(0,0,-2.5) rot=(0,0,1;0rad)
  Refine = true
  Relative = true
  Support = -> [Sketch001[Edge13,Edge11,Edge12]]
  _Version = 2
FEATURE [PartDesign::Hole] Hole002
  BaseFeature = -> Pad001
  CustomThreadClearance = 0
  Depth = 3
  DepthType = 0
  Diameter = 3.5
  DrillForDepth = false
  DrillPoint = 1
  DrillPointAngle = 118
  HoleCutCountersinkAngle = 90
  HoleCutCustomValues = false
  HoleCutDepth = 0
  HoleCutDiameter = 6.1
  HoleCutType = 0
  ModelThread = false
  Profile = -> Binder005
  Refine = true
  Reversed = true
  Suppressed = false
  Tapered = false
  TaperedAngle = 90
  ThreadClass = 0
  ThreadDepth = 3
  ThreadDepthType = 0
  ThreadDirection = 0
  ThreadFit = 0
  ThreadSize = 0
  ThreadType = 0
  Threaded = false
  UseCustomThreadClearance = false
  expr: Diameter = <<Vars>>.nut_inserts_m2
FEATURE [PartDesign::Chamfer] Chamfer
  Angle = 45
  Base = -> Hole002 [Edge33,Edge34,Edge31]
  BaseFeature = -> Hole002
  ChamferType = 0
  FlipDirection = false
  Refine = true
  Size = 1
  Size2 = 1
  SupportTransform = false
  Suppressed = false
  UseAllEdges = false
FEATURE [PartDesign::Body] Body  label="Top Enclosure Display Back"
  AllowCompound = false
  Group = -> [Binder002,Binder001,Binder,Pad,Hole,MultiTransform,Mirrored,Mirrored001,Hole001,Mirrored002,Sketch,Binder003,Pocket,Mirrored003,Sketch001,Binder004,Sketch002,Pad001,Binder005,Hole002,Chamfer]
  Origin = -> Origin
  Tip = -> Chamfer
---- part TopEnclosureDisplayFront.FCStd = doc fcstd_d4a49ea3fe33 ----
FCSTD DOCUMENT  (FreeCAD 1.0R39319 (Git))
Label: TopEnclosureDisplayFront
License: All rights reserved
LicenseURL: https://en.wikipedia.org/wiki/All_rights_reserved
objects: PartDesign::SubShapeBinder×5, PartDesign::Mirrored×3, App::Link×2, PartDesign::Pocket×2, PartDesign::Hole×2, PartDesign::Pad×1, PartDesign::MultiTransform×1, PartDesign::Chamfer×1, PartDesign::Body×1
note: 32 computed .brp shape members not serialized (recipe doc carries the construction recipe); baked Part::Feature solids carry a one-line shape summary decoded from their .brp
EXTERNAL_REF file=TopEnclosure.FCStd obj=Sketch
EXTERNAL_REF file=Spec.FCStd obj=Spreadsheet

FEATURE [App::Link] Link  label="MasterSketch"
  LinkedObject = -> <external TopEnclosure.FCStd>#Sketch
FEATURE [PartDesign::SubShapeBinder] Binder
  BindCopyOnChange = 0
  BindMode = 0
  ClaimChildren = false
  Context = -> Body [Binder.]
  Fuse = false
  MakeFace = true
  OffsetFill = false
  OffsetIntersection = false
  OffsetJoinType = 0
  OffsetOpenResult = false
  PartialLoad = false
  Refine = true
  Relative = true
  Support = -> [Link[Edge10,Edge9,Edge11,Edge12,Edge13,Edge14,Edge15,Edge16]]
  _Version = 2
FEATURE [PartDesign::SubShapeBinder] Binder001
  BindCopyOnChange = 0
  BindMode = 0
  ClaimChildren = false
  Context = -> Body [Binder001.]
  Fuse = false
  MakeFace = true
  OffsetFill = false
  OffsetIntersection = false
  OffsetJoinType = 0
  OffsetOpenResult = false
  PartialLoad = false
  Refine = true
  Relative = true
  Support = -> [Link[Edge39]]
  _Version = 2
FEATURE [PartDesign::SubShapeBinder] Binder002
  BindCopyOnChange = 0
  BindMode = 0
  ClaimChildren = false
  Context = -> Body [Binder002.]
  Fuse = false
  MakeFace = true
  OffsetFill = false
  OffsetIntersection = false
  OffsetJoinType = 0
  OffsetOpenResult = false
  PartialLoad = false
  Refine = true
  Relative = true
  Support = -> [Link[Edge40]]
  _Version = 2
FEATURE [PartDesign::SubShapeBinder] Binder004
  BindCopyOnChange = 0
  BindMode = 0
  ClaimChildren = false
  Context = -> Body [Binder004.]
  Fuse = false
  MakeFace = true
  OffsetFill = false
  OffsetIntersection = false
  OffsetJoinType = 0
  OffsetOpenResult = false
  PartialLoad = false
  Refine = true
  Relative = true
  Support = -> [Link[Edge35,Edge36,Edge33,Edge34]]
  _Version = 2
FEATURE [PartDesign::SubShapeBinder] Binder005
  BindCopyOnChange = 0
  BindMode = 0
  ClaimChildren = false
  Context = -> Body [Binder005.]
  Fuse = false
  MakeFace = true
  OffsetFill = false
  OffsetIntersection = false
  OffsetJoinType = 0
  OffsetOpenResult = false
  PartialLoad = false
  Refine = true
  Relative = true
  Support = -> [Link[Edge26,Edge25,Edge27,Edge32,Edge31,Edge28,Edge29,Edge30]]
  _Version = 2
FEATURE [App::Link] Link001  label="Vars"
  LinkedObject = -> <external Spec.FCStd>#Spreadsheet
FEATURE [PartDesign::Pad] Pad
  Direction = (0,0,1)
  Length = 6.5
  Length2 = 10
  Profile = -> Binder
  Refine = true
  Suppressed = false
  Type = 0
  expr: Length = <<Vars>>.display_depth + <<Vars>>.top_enclosure_front_depth
FEATURE [PartDesign::Pocket] Pocket
  BaseFeature = -> Pad
  Direction = (0,0,-1)
  Length = 5
  Length2 = 5
  Profile = -> Binder005
  Refine = true
  Reversed = true
  Suppressed = false
  Type = 1
FEATURE [PartDesign::Pocket] Pocket001
  BaseFeature = -> Pocket
  Direction = (0,0,-1)
  Length = 5.5
  Length2 = 5
  Profile = -> Binder004
  Refine = true
  Reversed = true
  Suppressed = false
  Type = 0
  expr: Length = <<Vars>>.display_depth
FEATURE [PartDesign::Hole] Hole
  BaseFeature = -> Pocket001
  CustomThreadClearance = 0
  Depth = 25
  DepthType = 0
  Diameter = 3.6
  DrillForDepth = false
  DrillPoint = 1
  DrillPointAngle = 118
  HoleCutCountersinkAngle = 90
  HoleCutCustomValues = false
  HoleCutDepth = 0
  HoleCutDiameter = 6.1
  HoleCutType = 0
  ModelThread = false
  Profile = -> Binder001
  Refine = true
  Reversed = true
  Suppressed = false
  Tapered = false
  TaperedAngle = 90
  ThreadClass = 0
  ThreadDepth = 25
  ThreadDepthType = 0
  ThreadDirection = 0
  ThreadFit = 2
  ThreadSize = 9
  ThreadType = 1
  Threaded = false
  UseCustomThreadClearance = false
FEATURE [PartDesign::Mirrored] Mirrored
  MirrorPlane = -> YZ_Plane
  Refine = true
  Suppressed = false
  TransformMode = 0
FEATURE [PartDesign::Mirrored] Mirrored001
  MirrorPlane = -> XZ_Plane
  Refine = true
  Suppressed = false
  TransformMode = 0
FEATURE [PartDesign::MultiTransform] MultiTransform
  BaseFeature = -> Hole
  Originals = -> [Hole]
  Refine = true
  Suppressed = false
  TransformMode = 0
  Transformations = -> [Mirrored,Mirrored001]
FEATURE [PartDesign::Hole] Hole001
  BaseFeature = -> MultiTransform
  CustomThreadClearance = 0
  Depth = 25
  DepthType = 0
  Diameter = 3.6
  DrillForDepth = false
  DrillPoint = 1
  DrillPointAngle = 118
  HoleCutCountersinkAngle = 90
  HoleCutCustomValues = false
  HoleCutDepth = 0
  HoleCutDiameter = 6.1
  HoleCutType = 0
  ModelThread = false
  Profile = -> Binder002
  Refine = true
  Reversed = true
  Suppressed = false
  Tapered = false
  TaperedAngle = 90
  ThreadClass = 0
  ThreadDepth = 25
  ThreadDepthType = 0
  ThreadDirection = 0
  ThreadFit = 2
  ThreadSize = 9
  ThreadType = 1
  Threaded = false
  UseCustomThreadClearance = false
FEATURE [PartDesign::Mirrored] Mirrored002
  BaseFeature = -> Hole001
  MirrorPlane = -> XZ_Plane
  Originals = -> [Hole001]
  Refine = true
  Suppressed = false
  TransformMode = 0
FEATURE [PartDesign::Chamfer] Chamfer
  Angle = 45
  Base = -> Mirrored002 [Edge39]
  BaseFeature = -> Mirrored002
  ChamferType = 0
  FlipDirection = false
  Refine = true
  Size = 0.5
  Size2 = 1
  SupportTransform = false
  Suppressed = false
  UseAllEdges = false
FEATURE [PartDesign::Body] Body  label="Top Enclosure Display Front"
  AllowCompound = false
  Group = -> [Binder,Binder001,Binder002,Binder004,Binder005,Pad,Pocket,Pocket001,Hole,MultiTransform,Mirrored,Mirrored001,Hole001,Mirrored002,Chamfer]
  Origin = -> Origin
  Tip = -> Chamfer
---- part TopEnclosureHood_v2.FCStd = doc fcstd_baf8cbb0d794 ----
FCSTD DOCUMENT  (FreeCAD 1.0R39319 (Git))
Label: TopEnclosureHood_v2
License: All rights reserved
LicenseURL: https://en.wikipedia.org/wiki/All_rights_reserved
objects: PartDesign::SubShapeBinder×6, Sketcher::SketchObject×4, PartDesign::Pad×4, PartDesign::Mirrored×3, App::Link×2, PartDesign::Hole×2, App::VarSet×1, PartDesign::MultiTransform×1, PartDesign::Pocket×1, PartDesign::Body×1
note: 44 computed .brp shape members not serialized (recipe doc carries the construction recipe); baked Part::Feature solids carry a one-line shape summary decoded from their .brp
EXTERNAL_REF file=TopEnclosure.FCStd obj=Sketch
EXTERNAL_REF file=Spec.FCStd obj=Spreadsheet

FEATURE [App::Link] Link  label="MasterSketch"
  LinkedObject = -> <external TopEnclosure.FCStd>#Sketch
FEATURE [PartDesign::SubShapeBinder] Binder
  BindCopyOnChange = 0
  BindMode = 0
  ClaimChildren = false
  Context = -> Body [Binder.]
  Fuse = false
  MakeFace = true
  OffsetFill = false
  OffsetIntersection = false
  OffsetJoinType = 0
  OffsetOpenResult = false
  PartialLoad = false
  Refine = true
  Relative = true
  Support = -> [Link[Edge17,Edge24,Edge18,Edge2,Edge1,Edge3,Edge19,Edge20]]
  _Version = 2
FEATURE [PartDesign::SubShapeBinder] Binder001
  BindCopyOnChange = 0
  BindMode = 0
  ClaimChildren = false
  Context = -> Body [Binder001.]
  Fuse = false
  MakeFace = true
  OffsetFill = false
  OffsetIntersection = false
  OffsetJoinType = 0
  OffsetOpenResult = false
  PartialLoad = false
  Refine = true
  Relative = true
  Support = -> [Link[Edge37]]
  _Version = 2
FEATURE [Sketcher::SketchObject] Sketch
  ArcFitTolerance = 1e-06
  AttachmentOffset = pos=(0,0,3.1) rot=(0,0,1;0rad)
  AttachmentSupport = -> [XY_Plane]
  ExternalGeometry = -> [Binder,Binder001]
  FullyConstrained = true
  MakeInternals = false
  MapMode = 5
  Placement = pos=(0,0,3.1) rot=(0,0,1;0rad)
  expr: .AttachmentOffset.Base.z = <<LocalVars>>.bottom_offset
  sketch-geometry (4):
    g0: LineSegment StartX=-137.5 StartY=40 StartZ=0 EndX=-137.5 EndY=35.205 EndZ=0
    g1: LineSegment StartX=-130 StartY=47.5 StartZ=0 EndX=-125.205 EndY=47.5 EndZ=0
    g2: ArcOfCircle CenterX=-137.703 CenterY=47.7033 CenterZ=0 NormalX=0 NormalY=0 NormalZ=1 AngleXU=0 Radius=12.5 StartAngle=4.72865 EndAngle=6.26692
    g3: ArcOfCircle CenterX=-130 CenterY=40 CenterZ=0 NormalX=0 NormalY=0 NormalZ=1 AngleXU=0 Radius=7.5 StartAngle=1.5708 EndAngle=3.14159
  constraints (9):
    c: Coincident(g0,g-3)
    c: PointOnObject(g0,g-4)
    c: Vertical(g0)
    c: Coincident(g1,g-3)
    c: Tangent(g3,g0) = -1.5708
    c: Coincident(g1,g2)
    c: Coincident(g0,g2)
    c: Tangent(g3,g1) = 1.5708
    c: Coincident(g2,g-4)
FEATURE [PartDesign::SubShapeBinder] Binder002
  BindCopyOnChange = 0
  BindMode = 0
  ClaimChildren = false
  Context = -> Body [Binder002.]
  Fuse = false
  MakeFace = true
  OffsetFill = false
  OffsetIntersection = false
  OffsetJoinType = 0
  OffsetOpenResult = false
  PartialLoad = false
  Refine = true
  Relative = true
  Support = -> [Link[Edge39]]
  _Version = 2
FEATURE [PartDesign::SubShapeBinder] Binder003
  BindCopyOnChange = 0
  BindMode = 0
  ClaimChildren = false
  Context = -> Body [Binder003.]
  Fuse = false
  MakeFace = true
  OffsetFill = false
  OffsetIntersection = false
  OffsetJoinType = 0
  OffsetOpenResult = false
  PartialLoad = false
  Refine = true
  Relative = true
  Support = -> [Link[Edge38]]
  _Version = 2
FEATURE [PartDesign::SubShapeBinder] Binder004
  BindCopyOnChange = 0
  BindMode = 0
  ClaimChildren = false
  Context = -> Body [Binder004.]
  Fuse = false
  MakeFace = true
  OffsetFill = false
  OffsetIntersection = false
  OffsetJoinType = 0
  OffsetOpenResult = false
  PartialLoad = false
  Refine = true
  Relative = true
  Support = -> [Link[Edge40]]
  _Version = 2
FEATURE [Sketcher::SketchObject] Sketch001
  ArcFitTolerance = 1e-06
  AttachmentOffset = pos=(0,0,3.1) rot=(0,0,1;0rad)
  AttachmentSupport = -> [XY_Plane]
  ExternalGeometry = -> [Binder,Binder003]
  FullyConstrained = true
  MakeInternals = false
  MapMode = 5
  Placement = pos=(0,0,3.1) rot=(0,0,1;0rad)
  expr: .AttachmentOffset.Base.z = <<LocalVars>>.bottom_offset
  sketch-geometry (2):
    g0: LineSegment StartX=12.2674 StartY=47.5 StartZ=0 EndX=-12.2674 EndY=47.5 EndZ=0
    g1: ArcOfCircle CenterX=0 CenterY=49.9 CenterZ=0 NormalX=0 NormalY=0 NormalZ=1 AngleXU=0 Radius=12.5 StartAngle=3.33479 EndAngle=6.08999
  constraints (6):
    c: PointOnObject(g0,g-3)
    c: PointOnObject(g0,g-3)
    c: Coincident(g1,g-4)
    c: PointOnObject(g1,g-4)
    c: Coincident(g1,g0)
    c: Coincident(g0,g1)
FEATURE [App::Link] Link001  label="Vars"
  LinkedObject = -> <external Spec.FCStd>#Spreadsheet
FEATURE [PartDesign::Pad] Pad
  Direction = (0,0,1)
  Length = 12.5
  Length2 = 10
  Profile = -> Binder
  Refine = true
  Suppressed = false
  Type = 0
FEATURE [PartDesign::Mirrored] Mirrored
  MirrorPlane = -> YZ_Plane
  Refine = true
  Suppressed = false
  TransformMode = 0
FEATURE [PartDesign::Mirrored] Mirrored001
  MirrorPlane = -> XZ_Plane
  Refine = true
  Suppressed = false
  TransformMode = 0
FEATURE [Sketcher::SketchObject] Sketch002
  ArcFitTolerance = 1e-06
  AttachmentSupport = -> [YZ_Plane]
  FullyConstrained = true
  MakeInternals = false
  MapMode = 5
  Placement = pos=(0,0,0) rot=(0.57735,0.57735,0.57735;2.0944rad)
  expr: Constraints[13] = <<Vars>>.hood_angle
  expr: Constraints[4] = <<Vars>>.top_enclosure_height
  sketch-geometry (5):
    g0: LineSegment StartX=50 StartY=0 StartZ=0 EndX=50 EndY=12.5 EndZ=0
    g1: LineSegment StartX=-50 StartY=0 StartZ=0 EndX=-50 EndY=5.50732 EndZ=0
    g2: LineSegment StartX=-50 StartY=5.50732 StartZ=0 EndX=50 EndY=12.5 EndZ=0
    g3: LineSegment StartX=-50 StartY=5.50732 StartZ=0 EndX=-50 EndY=12.5 EndZ=0
    g4: LineSegment StartX=-50 StartY=12.5 StartZ=0 EndX=50 EndY=12.5 EndZ=0
  constraints (14):
    c: PointOnObject(g0,g-1)
    c: Vertical(g0)
    c: Vertical(g1)
    c: Symmetric(g1,g0,g-2)
    c: DistanceX(g1,g0) = 100
    c: DistanceY(g0,g0) = 12.5
    c: Coincident(g2,g1)
    c: Coincident(g2,g0)
    c: Coincident(g3,g1)
    c: Coincident(g4,g3)
    c: Coincident(g4,g0)
    c: Horizontal(g4)
    c: Vertical(g3)
    c: Angle(g4,g2) = 0.0698132
FEATURE [PartDesign::SubShapeBinder] Binder005
  BindCopyOnChange = 0
  BindMode = 0
  ClaimChildren = false
  Context = -> Body [Binder005.]
  Fuse = false
  MakeFace = true
  OffsetFill = false
  OffsetIntersection = false
  OffsetJoinType = 0
  OffsetOpenResult = false
  PartialLoad = false
  Refine = true
  Relative = true
  Support = -> [Sketch002[Edge2,Edge5,Edge4]]
  _Version = 2
FEATURE [App::VarSet] VarSet  label="LocalVars"
  bottom_offset = 3.1
  expr: bottom_offset = <<Vars>>.wall + <<Vars>>.clearance * 3
FEATURE [Sketcher::SketchObject] Sketch003
  ArcFitTolerance = 1e-06
  AttachmentOffset = pos=(0,0,3.1) rot=(0,0,1;0rad)
  AttachmentSupport = -> [XY_Plane]
  ExternalGeometry = -> [Binder]
  FullyConstrained = true
  MakeInternals = false
  MapMode = 5
  Placement = pos=(0,0,3.1) rot=(0,0,1;0rad)
  expr: .AttachmentOffset.Base.z = <<LocalVars>>.bottom_offset
  sketch-geometry (18):
    g0: LineSegment StartX=137.5 StartY=-40 StartZ=0 EndX=137.5 EndY=40 EndZ=0
    g1: LineSegment StartX=130 StartY=47.5 StartZ=0 EndX=-130 EndY=47.5 EndZ=0
    g2: LineSegment StartX=-137.5 StartY=40 StartZ=0 EndX=-137.5 EndY=-40 EndZ=0
    g3: LineSegment StartX=-130 StartY=-47.5 StartZ=0 EndX=130 EndY=-47.5 EndZ=0
    g4: ArcOfCircle CenterX=130 CenterY=-40 CenterZ=0 NormalX=0 NormalY=0 NormalZ=1 AngleXU=0 Radius=7.5 StartAngle=4.71239 EndAngle=6.28319
    g5: ArcOfCircle CenterX=130 CenterY=40 CenterZ=0 NormalX=0 NormalY=0 NormalZ=1 AngleXU=0 Radius=7.5 StartAngle=3e-16 EndAngle=1.5708
    g6: ArcOfCircle CenterX=-130 CenterY=40 CenterZ=0 NormalX=0 NormalY=0 NormalZ=1 AngleXU=0 Radius=7.5 StartAngle=1.5708 EndAngle=3.14159
    g7: ArcOfCircle CenterX=-130 CenterY=-40 CenterZ=0 NormalX=0 NormalY=0 NormalZ=1 AngleXU=0 Radius=7.5 StartAngle=3.14159 EndAngle=4.71239
    g8: LineSegment StartX=135.5 StartY=-40 StartZ=0 EndX=135.5 EndY=40 EndZ=0
    g9: LineSegment StartX=130 StartY=45.5 StartZ=0 EndX=-130 EndY=45.5 EndZ=0
    g10: LineSegment StartX=-135.5 StartY=40 StartZ=0 EndX=-135.5 EndY=-40 EndZ=0
    g11: LineSegment StartX=-130 StartY=-45.5 StartZ=0 EndX=130 EndY=-45.5 EndZ=0
    g12: ArcOfCircle CenterX=130 CenterY=-40 CenterZ=0 NormalX=0 NormalY=0 NormalZ=1 AngleXU=0 Radius=5.5 StartAngle=4.71239 EndAngle=6.28319
    g13: ArcOfCircle CenterX=130 CenterY=40 CenterZ=0 NormalX=0 NormalY=0 NormalZ=1 AngleXU=0 Radius=5.5 StartAngle=-9e-16 EndAngle=1.5708
    g14: ArcOfCircle CenterX=-130 CenterY=40 CenterZ=0 NormalX=0 NormalY=0 NormalZ=1 AngleXU=0 Radius=5.5 StartAngle=1.5708 EndAngle=3.14159
    g15: ArcOfCircle CenterX=-130 CenterY=-40 CenterZ=0 NormalX=0 NormalY=0 NormalZ=1 AngleXU=0 Radius=5.5 StartAngle=3.14159 EndAngle=4.71239
    g16: GeomPoint [constr] X=-137.5 Y=47.5 Z=0
    g17: GeomPoint [constr] X=0 Y=0 Z=0
  constraints (37):
    c: Tangent(g0,g4) = -1.5708
    c: Tangent(g0,g5) = -1.5708
    c: Tangent(g1,g5) = -1.5708
    c: Tangent(g1,g6) = -1.5708
    c: Tangent(g2,g6) = -1.5708
    c: Tangent(g2,g7) = -1.5708
    c: Tangent(g3,g7) = -1.5708
    c: Tangent(g3,g4) = -1.5708
    c: Vertical(g0)
    c: Vertical(g2)
    c: Horizontal(g1)
    c: Horizontal(g3)
    c: Equal(g4,g5)
    c: Equal(g5,g6)
    c: Equal(g6,g7)
    c: Tangent(g8,g12) = -1.5708
    c: Tangent(g8,g13) = -1.5708
    c: Tangent(g9,g13) = -1.5708
    c: Tangent(g9,g14) = -1.5708
    c: Tangent(g10,g14) = -1.5708
    c: Tangent(g10,g15) = -1.5708
    c: Tangent(g11,g15) = -1.5708
    c: Tangent(g11,g12) = -1.5708
    c: Coincident(g4,g12)
    c: Coincident(g5,g13)
    c: Coincident(g6,g14)
    c: Coincident(g7,g15)
    c: Vertical(g8)
    c: Vertical(g10)
    c: Horizontal(g9)
    c: Symmetric(g2,g0,g17)
    c: PointOnObject(g16,g1)
    c: PointOnObject(g16,g2)
    c: Coincident(g17,g-1)
    c: Coincident(g6,g-3)
    c: Equal(g6,g-3)
    c: DistanceY(g9,g1) = 2
FEATURE [PartDesign::Pad] Pad003
  BaseFeature = -> Pad
  Direction = (0,0,1)
  Length = 2.5
  Length2 = 10
  Profile = -> Sketch003
  ReferenceAxis = -> Sketch003 [N_Axis]
  Refine = true
  Suppressed = false
  Type = 0
  expr: Length = <<Vars>>.wall
FEATURE [PartDesign::Pad] Pad001
  BaseFeature = -> Pad003
  Direction = (0,0,1)
  Length = 2.5
  Length2 = 10
  Profile = -> Sketch
  ReferenceAxis = -> Sketch [N_Axis]
  Refine = true
  Suppressed = false
  Type = 0
  expr: Length = <<Vars>>.wall
FEATURE [PartDesign::Hole] Hole
  BaseFeature = -> Pad001
  CustomThreadClearance = 0
  Depth = 601.12
  DepthType = 1
  Diameter = 3.6
  DrillForDepth = false
  DrillPoint = 1
  DrillPointAngle = 118
  HoleCutCountersinkAngle = 90
  HoleCutCustomValues = false
  HoleCutDepth = 0
  HoleCutDiameter = 6.1
  HoleCutType = 0
  ModelThread = false
  Profile = -> Binder002
  Refine = true
  Reversed = true
  Suppressed = false
  Tapered = false
  TaperedAngle = 90
  ThreadClass = 0
  ThreadDepth = 601.12
  ThreadDepthType = 0
  ThreadDirection = 0
  ThreadFit = 2
  ThreadSize = 9
  ThreadType = 1
  Threaded = false
  UseCustomThreadClearance = false
FEATURE [PartDesign::MultiTransform] MultiTransform
  BaseFeature = -> Hole
  Originals = -> [Pad001,Hole]
  Refine = true
  Suppressed = false
  TransformMode = 0
  Transformations = -> [Mirrored,Mirrored001]
FEATURE [PartDesign::Pad] Pad002
  BaseFeature = -> MultiTransform
  Direction = (0,0,1)
  Length = 2.5
  Length2 = 10
  Profile = -> Sketch001
  ReferenceAxis = -> Sketch001 [N_Axis]
  Refine = true
  Suppressed = false
  Type = 0
  expr: Length = <<Vars>>.wall
FEATURE [PartDesign::Hole] Hole001
  BaseFeature = -> Pad002
  CustomThreadClearance = 0
  Depth = 25
  DepthType = 0
  Diameter = 3.6
  DrillForDepth = false
  DrillPoint = 1
  DrillPointAngle = 118
  HoleCutCountersinkAngle = 90
  HoleCutCustomValues = false
  HoleCutDepth = 0
  HoleCutDiameter = 6.1
  HoleCutType = 0
  ModelThread = false
  Profile = -> Binder004
  Refine = true
  Reversed = true
  Suppressed = false
  Tapered = false
  TaperedAngle = 90
  ThreadClass = 0
  ThreadDepth = 25
  ThreadDepthType = 0
  ThreadDirection = 0
  ThreadFit = 2
  ThreadSize = 9
  ThreadType = 1
  Threaded = false
  UseCustomThreadClearance = false
FEATURE [PartDesign::Mirrored] Mirrored002
  BaseFeature = -> Hole001
  MirrorPlane = -> XZ_Plane
  Originals = -> [Pad002,Hole001]
  Refine = true
  Suppressed = false
  TransformMode = 0
FEATURE [PartDesign::Pocket] Pocket
  BaseFeature = -> Mirrored002
  Direction = (-1,0,0)
  Length = 5
  Length2 = 5
  Midplane = true
  Profile = -> Binder005
  Refine = true
  Suppressed = false
  Type = 1
FEATURE [PartDesign::Body] Body  label="Top Enclosure Hood"
  AllowCompound = false
  Group = -> [Binder,Sketch,Binder001,Binder002,Binder003,Binder004,Sketch001,Pad,Pad003,Pad001,Hole,MultiTransform,Mirrored,Mirrored001,Pad002,Hole001,Mirrored002,Sketch002,Binder005,Pocket,Sketch003]
  Origin = -> Origin
  Tip = -> Pocket
---- part TopEnclosureShell.FCStd = doc fcstd_e799acd3cff3 ----
FCSTD DOCUMENT  (FreeCAD 1.0R39319 (Git))
Label: TopEnclosureShell
License: All rights reserved
LicenseURL: https://en.wikipedia.org/wiki/All_rights_reserved
objects: PartDesign::SubShapeBinder×20, Sketcher::SketchObject×9, PartDesign::Mirrored×8, PartDesign::Body×8, PartDesign::Pocket×6, PartDesign::Pad×5, PartDesign::Boolean×5, PartDesign::Hole×4, Part::FeaturePython×3, App::Link×2, PartDesign::MultiTransform×1, Part::Extrusion×1, App::DocumentObjectGroup×1, App::VarSet×1
note: 123 computed .brp shape members not serialized (recipe doc carries the construction recipe); baked Part::Feature solids carry a one-line shape summary decoded from their .brp
EXTERNAL_REF file=Spec.FCStd obj=Spreadsheet
EXTERNAL_REF file=TopEnclosure.FCStd obj=Sketch

FEATURE [App::Link] Link  label="Vars"
  LinkedObject = -> <external Spec.FCStd>#Spreadsheet
FEATURE [App::Link] Link001  label="MasterSketch"
  LinkedObject = -> <external TopEnclosure.FCStd>#Sketch
FEATURE [PartDesign::SubShapeBinder] Binder
  BindCopyOnChange = 0
  BindMode = 0
  ClaimChildren = false
  Context = -> Body [Binder.]
  Fuse = false
  MakeFace = true
  OffsetFill = false
  OffsetIntersection = false
  OffsetJoinType = 0
  OffsetOpenResult = false
  PartialLoad = false
  Refine = true
  Relative = true
  Support = -> [Link001[Edge17,Edge1,Edge2,Edge18,Edge3,Edge19,Edge20,Edge4]]
  _Version = 2
FEATURE [PartDesign::Pad] Pad
  Direction = (0,0,1)
  Length = 14
  Length2 = 10
  Profile = -> Binder
  Refine = true
  Suppressed = false
  Type = 0
  expr: Length = <<Vars>>.top_enclosure_depth
FEATURE [PartDesign::SubShapeBinder] Binder001
  BindCopyOnChange = 0
  BindMode = 0
  ClaimChildren = false
  Context = -> Body [Binder001.]
  Fuse = false
  MakeFace = true
  OffsetFill = false
  OffsetIntersection = false
  OffsetJoinType = 0
  OffsetOpenResult = false
  PartialLoad = false
  Refine = true
  Relative = true
  Support = -> [Link001[Edge37,Edge39]]
  _Version = 2
FEATURE [Sketcher::SketchObject] Sketch
  ArcFitTolerance = 1e-06
  AttachmentOffset = pos=(0,0,2.5) rot=(0,0,1;0rad)
  AttachmentSupport = -> [XY_Plane]
  ExternalGeometry = -> [Binder001]
  FullyConstrained = true
  MakeInternals = false
  MapMode = 5
  Placement = pos=(0,0,2.5) rot=(0,0,1;0rad)
  expr: .AttachmentOffset.Base.z = <<LocalVars>>.bottom_offset
  sketch-geometry (4):
    g0: ArcOfCircle CenterX=-137.703 CenterY=47.7033 CenterZ=0 NormalX=0 NormalY=0 NormalZ=1 AngleXU=0 Radius=12.5 StartAngle=4.72865 EndAngle=6.26692
    g1: LineSegment StartX=-137.5 StartY=35.205 StartZ=0 EndX=-137.5 EndY=41.4 EndZ=0
    g2: LineSegment StartX=-125.205 StartY=47.5 StartZ=0 EndX=-131.4 EndY=47.5 EndZ=0
    g3: ArcOfCircle CenterX=-131.4 CenterY=41.4 CenterZ=0 NormalX=0 NormalY=0 NormalZ=1 AngleXU=0 Radius=6.1 StartAngle=1.5708 EndAngle=3.14159
  constraints (10):
    c: Coincident(g0,g-4)
    c: PointOnObject(g0,g-4)
    c: Horizontal(g-3,g0)
    c: Vertical(g-3,g0)
    c: Coincident(g1,g0)
    c: Coincident(g1,g-3)
    c: Coincident(g2,g0)
    c: Coincident(g2,g-3)
    c: Coincident(g3,g1)
    c: Tangent(g3,g2) = -1.5708
FEATURE [PartDesign::SubShapeBinder] Binder002
  BindCopyOnChange = 0
  BindMode = 0
  ClaimChildren = false
  Context = -> Body [Binder002.]
  Fuse = false
  MakeFace = true
  OffsetFill = false
  OffsetIntersection = false
  OffsetJoinType = 0
  OffsetOpenResult = false
  PartialLoad = false
  Refine = true
  Relative = true
  Support = -> [Link001[Edge38,Edge40]]
  _Version = 2
FEATURE [PartDesign::Pad] Pad001
  BaseFeature = -> Pad
  Direction = (0,0,1)
  Length = 6.5
  Length2 = 10
  Profile = -> Sketch
  ReferenceAxis = -> Sketch [N_Axis]
  Refine = true
  Suppressed = false
  Type = 0
  expr: Length = <<LocalVars>>.internal_depth
FEATURE [PartDesign::SubShapeBinder] Binder003
  BindCopyOnChange = 0
  BindMode = 0
  ClaimChildren = false
  Context = -> Body [Binder003.]
  Fuse = false
  MakeFace = true
  OffsetFill = false
  OffsetIntersection = false
  OffsetJoinType = 0
  OffsetOpenResult = false
  PartialLoad = false
  Refine = true
  Relative = true
  Support = -> [Binder001[Edge2]]
  _Version = 2
FEATURE [PartDesign::Hole] Hole
  BaseFeature = -> Pad001
  CustomThreadClearance = 0
  Depth = 25
  DepthType = 0
  Diameter = 4.5
  DrillForDepth = false
  DrillPoint = 1
  DrillPointAngle = 118
  HoleCutCountersinkAngle = 90
  HoleCutCustomValues = false
  HoleCutDepth = 0
  HoleCutDiameter = 6.1
  HoleCutType = 0
  ModelThread = false
  Profile = -> Binder003
  Refine = true
  Reversed = true
  Suppressed = false
  Tapered = false
  TaperedAngle = 90
  ThreadClass = 0
  ThreadDepth = 25
  ThreadDepthType = 0
  ThreadDirection = 0
  ThreadFit = 0
  ThreadSize = 0
  ThreadType = 0
  Threaded = false
  UseCustomThreadClearance = false
  expr: Diameter = <<Vars>>.nut_inserts_m3
FEATURE [PartDesign::Mirrored] Mirrored
  MirrorPlane = -> YZ_Plane
  Refine = true
  Suppressed = false
  TransformMode = 0
FEATURE [PartDesign::Mirrored] Mirrored001
  MirrorPlane = -> XZ_Plane
  Refine = true
  Suppressed = false
  TransformMode = 0
FEATURE [PartDesign::MultiTransform] MultiTransform
  BaseFeature = -> Hole
  Originals = -> [Pad001,Hole]
  Refine = true
  Suppressed = false
  TransformMode = 0
  Transformations = -> [Mirrored,Mirrored001]
FEATURE [Sketcher::SketchObject] Sketch001
  ArcFitTolerance = 1e-06
  AttachmentOffset = pos=(0,0,2.5) rot=(0,0,1;0rad)
  AttachmentSupport = -> [XY_Plane]
  ExternalGeometry = -> [Binder002]
  FullyConstrained = true
  MakeInternals = false
  MapMode = 5
  Placement = pos=(0,0,2.5) rot=(0,0,1;0rad)
  expr: .AttachmentOffset.Base.z = <<LocalVars>>.bottom_offset
  sketch-geometry (2):
    g0: ArcOfCircle CenterX=0 CenterY=49.9 CenterZ=0 NormalX=0 NormalY=0 NormalZ=1 AngleXU=0 Radius=12.5 StartAngle=3.33479 EndAngle=6.08999
    g1: LineSegment StartX=-12.2674 StartY=47.5 StartZ=0 EndX=12.2674 EndY=47.5 EndZ=0
  constraints (6):
    c: Coincident(g0,g-3)
    c: PointOnObject(g0,g-3)
    c: Horizontal(g1)
    c: PointOnObject(g1,g-4)
    c: Coincident(g1,g0)
    c: Coincident(g1,g0)
FEATURE [PartDesign::Pad] Pad002
  BaseFeature = -> MultiTransform
  Direction = (0,0,1)
  Length = 6.5
  Length2 = 10
  Profile = -> Sketch001
  ReferenceAxis = -> Sketch001 [N_Axis]
  Refine = true
  Suppressed = false
  Type = 0
  expr: Length = <<LocalVars>>.internal_depth
FEATURE [PartDesign::SubShapeBinder] Binder004
  BindCopyOnChange = 0
  BindMode = 0
  ClaimChildren = false
  Context = -> Body [Binder004.]
  Fuse = false
  MakeFace = true
  OffsetFill = false
  OffsetIntersection = false
  OffsetJoinType = 0
  OffsetOpenResult = false
  PartialLoad = false
  Refine = true
  Relative = true
  Support = -> [Binder002[Edge2]]
  _Version = 2
FEATURE [PartDesign::Hole] Hole001
  BaseFeature = -> Pad002
  CustomThreadClearance = 0
  Depth = 25
  DepthType = 0
  Diameter = 4.5
  DrillForDepth = false
  DrillPoint = 1
  DrillPointAngle = 118
  HoleCutCountersinkAngle = 90
  HoleCutCustomValues = false
  HoleCutDepth = 0
  HoleCutDiameter = 6.1
  HoleCutType = 0
  ModelThread = false
  Profile = -> Binder004
  Refine = true
  Reversed = true
  Suppressed = false
  Tapered = false
  TaperedAngle = 90
  ThreadClass = 0
  ThreadDepth = 25
  ThreadDepthType = 0
  ThreadDirection = 0
  ThreadFit = 0
  ThreadSize = 0
  ThreadType = 0
  Threaded = false
  UseCustomThreadClearance = false
  expr: Diameter = <<Vars>>.nut_inserts_m3
FEATURE [PartDesign::Mirrored] Mirrored002
  BaseFeature = -> Hole001
  MirrorPlane = -> XZ_Plane
  Originals = -> [Pad002,Hole001]
  Refine = true
  Suppressed = false
  TransformMode = 0
FEATURE [PartDesign::Body] Body  label="Top Enclosure Shell - Base"
  AllowCompound = false
  Group = -> [Binder,Pad,Sketch,Binder001,Binder002,Pad001,Binder003,Hole,MultiTransform,Mirrored,Mirrored001,Sketch001,Pad002,Binder004,Hole001,Mirrored002]
  Origin = -> Origin
  Tip = -> Mirrored002
FEATURE [PartDesign::SubShapeBinder] Binder005
  BindCopyOnChange = 0
  BindMode = 0
  ClaimChildren = false
  Context = -> Body001 [Binder005.]
  Fuse = false
  MakeFace = true
  OffsetFill = false
  OffsetIntersection = false
  OffsetJoinType = 0
  OffsetOpenResult = false
  PartialLoad = false
  Refine = true
  Relative = true
  Support = -> [Body]
  _Version = 2
FEATURE [PartDesign::Boolean] Boolean
  Group = -> [Binder005]
  Refine = true
  Suppressed = false
  Type = 0
  UsePlacement = true
FEATURE [Sketcher::SketchObject] Sketch002
  ArcFitTolerance = 1e-06
  AttachmentSupport = -> [YZ_Plane001]
  FullyConstrained = true
  MakeInternals = false
  MapMode = 5
  Placement = pos=(0,0,0) rot=(0.57735,0.57735,0.57735;2.0944rad)
  expr: Constraints[2] = <<Vars>>.top_enclosure_height / 2
  expr: Constraints[3] = <<Vars>>.top_enclosure_depth
  sketch-geometry (12):
    g0: LineSegment StartX=-50 StartY=0 StartZ=0 EndX=-50 EndY=14 EndZ=0
    g1: LineSegment StartX=-50 StartY=14 StartZ=0 EndX=-57.275 EndY=22.8501 EndZ=0
    g2: LineSegment StartX=-50 StartY=0 StartZ=0 EndX=-68.5971 EndY=7.16934 EndZ=0
    g3: Circle CenterX=-65 CenterY=16.5 CenterZ=0 NormalX=0 NormalY=0 NormalZ=1 AngleXU=0 Radius=4.5
    g4: ArcOfCircle CenterX=-65 CenterY=16.5 CenterZ=0 NormalX=0 NormalY=0 NormalZ=1 AngleXU=0 Radius=10 StartAngle=0.688024 EndAngle=4.34444
    g5: LineSegment StartX=-65 StartY=22.85 StartZ=0 EndX=-70.4993 EndY=19.675 EndZ=0
    g6: LineSegment StartX=-70.4993 StartY=19.675 StartZ=0 EndX=-70.4993 EndY=13.325 EndZ=0
    g7: LineSegment StartX=-70.4993 StartY=13.325 StartZ=0 EndX=-65 EndY=10.15 EndZ=0
    g8: LineSegment StartX=-65 StartY=10.15 StartZ=0 EndX=-59.5007 EndY=13.325 EndZ=0
    g9: LineSegment StartX=-59.5007 StartY=13.325 StartZ=0 EndX=-59.5007 EndY=19.675 EndZ=0
    g10: LineSegment StartX=-59.5007 StartY=19.675 StartZ=0 EndX=-65 EndY=22.85 EndZ=0
    g11: Circle [constr] CenterX=-65 CenterY=16.5 CenterZ=0 NormalX=0 NormalY=0 NormalZ=1 AngleXU=0 Radius=6.35
  constraints (29):
    c: PointOnObject(g0,g-1)
    c: Vertical(g0)
    c: DistanceX(g0,g-1) = 50
    c: DistanceY(g0,g0) = 14
    c: Coincident(g1,g0)
    c: Coincident(g2,g0)
    c: Coincident(g4,g3)
    c: Tangent(g1,g4) = -1.5708
    c: Tangent(g2,g4) = 1.5708
    c: Diameter(g4) = 20
    c: DistanceX(g3,g0) = 15
    c: DistanceY(g0,g3) = 2.5
    c: Diameter(g3) = 9
    c: Coincident(g5,g6)
    c: Coincident(g6,g7)
    c: Coincident(g7,g8)
    c: Coincident(g8,g9)
    c: Coincident(g9,g10)
    c: Coincident(g10,g5)
    c: Equal(g5, g6-g10) x5
    c: PointOnObject(g5,g11)
    c: PointOnObject(g6,g11)
    c: PointOnObject(g7,g11)
    c: PointOnObject(g8,g11)
    c: PointOnObject(g9,g11)
    c: PointOnObject(g10,g11)
    c: Coincident(g11,g3)
    c: Vertical(g5,g3)
    c: DistanceY(g6,g6) = 6.35
FEATURE [PartDesign::SubShapeBinder] Binder006
  BindCopyOnChange = 0
  BindMode = 0
  ClaimChildren = false
  Context = -> Body001 [Binder006.]
  Fuse = false
  MakeFace = true
  OffsetFill = false
  OffsetIntersection = false
  OffsetJoinType = 0
  OffsetOpenResult = false
  PartialLoad = false
  Refine = true
  Relative = true
  Support = -> [Sketch002[Edge2,Edge3,Edge4,Edge1]]
  _Version = 2
FEATURE [PartDesign::Pad] Pad003
  BaseFeature = -> Boolean
  Direction = (1,0,0)
  Length = 216
  Length2 = 10
  Midplane = true
  Profile = -> Binder006
  Refine = true
  Suppressed = false
  Type = 0
  expr: Length = <<Vars>>.top_enclosure_width - 32 * 2
FEATURE [PartDesign::SubShapeBinder] Binder007
  BindCopyOnChange = 0
  BindMode = 0
  ClaimChildren = false
  Context = -> Body001 [Binder007.]
  Fuse = false
  MakeFace = true
  OffsetFill = false
  OffsetIntersection = false
  OffsetJoinType = 0
  OffsetOpenResult = false
  PartialLoad = false
  Placement = pos=(99,0,0) rot=(0,0,1;0rad)
  Refine = true
  Relative = true
  Support = -> [Sketch002[Edge5]]
  _Version = 2
  expr: .Placement.Base.x = <<Vars>>.top_enclosure_width / 2 - 32 - 9
FEATURE [PartDesign::SubShapeBinder] Binder008
  BindCopyOnChange = 0
  BindMode = 0
  ClaimChildren = false
  Context = -> Body001 [Binder008.]
  Fuse = false
  MakeFace = true
  OffsetFill = false
  OffsetIntersection = false
  OffsetJoinType = 0
  OffsetOpenResult = false
  PartialLoad = false
  Placement = pos=(99,0,0) rot=(0,0,1;0rad)
  Refine = true
  Relative = true
  Support = -> [Sketch002[Edge6,Edge11,Edge10,Edge9,Edge8,Edge7]]
  _Version = 2
  expr: .Placement.Base.x = <<Vars>>.top_enclosure_width / 2 - 32 - 9
FEATURE [PartDesign::Pocket] Pocket
  BaseFeature = -> Pad003
  Direction = (-1,0,0)
  Length = 5
  Length2 = 5
  Profile = -> Binder007
  Refine = true
  Reversed = true
  Suppressed = false
  Type = 1
FEATURE [PartDesign::Pocket] Pocket001
  BaseFeature = -> Pocket
  Direction = (-1,0,0)
  Length = 9
  Length2 = 5
  Profile = -> Binder008
  Refine = true
  Suppressed = false
  Type = 0
FEATURE [PartDesign::Mirrored] Mirrored003
  BaseFeature = -> Pocket001
  MirrorPlane = -> YZ_Plane001
  Originals = -> [Pocket,Pocket001]
  Refine = true
  Suppressed = false
  TransformMode = 0
FEATURE [PartDesign::Body] Body001  label="Top Enclosure Shell - 1"
  AllowCompound = false
  Group = -> [Boolean,Sketch002,Binder006,Pad003,Binder007,Binder008,Pocket,Pocket001,Mirrored003]
  Origin = -> Origin001
  Tip = -> Mirrored003
FEATURE [PartDesign::SubShapeBinder] Binder009
  BindCopyOnChange = 0
  BindMode = 0
  ClaimChildren = false
  Context = -> Body002 [Binder009.]
  Fuse = false
  MakeFace = true
  OffsetFill = false
  OffsetIntersection = false
  OffsetJoinType = 0
  OffsetOpenResult = false
  PartialLoad = false
  Refine = true
  Relative = true
  Support = -> [Body001]
  _Version = 2
FEATURE [PartDesign::Boolean] Boolean001
  Group = -> [Binder009]
  Refine = true
  Suppressed = false
  Type = 0
  UsePlacement = true
FEATURE [Sketcher::SketchObject] Sketch003
  ArcFitTolerance = 1e-06
  AttachmentSupport = -> [Boolean001]
  ExternalGeometry = -> [Boolean001]
  FullyConstrained = false
  MakeInternals = false
  MapMode = 5
  Placement = pos=(0,-47.5,0) rot=(0,0.707107,0.707107;3.14159rad)
  expr: Constraints[26] = <<Vars>>.wire_hole_offset_x
  expr: Constraints[28] = <<Vars>>.wire_hole_height
  expr: Constraints[4] = <<Vars>>.wire_hole_width
  sketch-geometry (13):
    g0: LineSegment StartX=25 StartY=9.5 StartZ=0 EndX=25 EndY=4.5 EndZ=0
    g1: LineSegment StartX=27 StartY=2.5 StartZ=0 EndX=53 EndY=2.5 EndZ=0
    g2: LineSegment StartX=55 StartY=4.5 StartZ=0 EndX=55 EndY=9.5 EndZ=0
    g3: LineSegment StartX=53 StartY=11.5 StartZ=0 EndX=27 EndY=11.5 EndZ=0
    g4: ArcOfCircle CenterX=27 CenterY=9.5 CenterZ=0 NormalX=0 NormalY=0 NormalZ=1 AngleXU=0 Radius=2 StartAngle=1.5708 EndAngle=3.14159
    g5: GeomPoint [constr] X=25 Y=11.5 Z=0
    g6: ArcOfCircle CenterX=27 CenterY=4.5 CenterZ=0 NormalX=0 NormalY=0 NormalZ=1 AngleXU=0 Radius=2 StartAngle=3.14159 EndAngle=4.71239
    g7: GeomPoint [constr] X=25 Y=2.5 Z=0
    g8: ArcOfCircle CenterX=53 CenterY=4.5 CenterZ=0 NormalX=0 NormalY=0 NormalZ=1 AngleXU=0 Radius=2 StartAngle=4.71239 EndAngle=6.28319
    g9: GeomPoint [constr] X=55 Y=2.5 Z=0
    g10: ArcOfCircle CenterX=53 CenterY=9.5 CenterZ=0 NormalX=0 NormalY=0 NormalZ=1 AngleXU=0 Radius=2 StartAngle=0 EndAngle=1.5708
    g11: GeomPoint [constr] X=55 Y=11.5 Z=0
    g12: GeomPoint X=40 Y=7 Z=0
  constraints (29):
    c: Vertical(g0)
    c: Vertical(g2)
    c: Horizontal(g1)
    c: Horizontal(g3)
    c: DistanceX(g5,g11) = 30
    c: PointOnObject(g5,g0)
    c: PointOnObject(g5,g3)
    c: Tangent(g0,g4) = -1.5708
    c: Tangent(g3,g4) = -1.5708
    c: PointOnObject(g7,g0)
    c: PointOnObject(g7,g1)
    c: Tangent(g0,g6) = -1.5708
    c: Tangent(g1,g6) = -1.5708
    c: PointOnObject(g9,g1)
    c: PointOnObject(g9,g2)
    c: Tangent(g1,g8) = -1.5708
    c: Tangent(g2,g8) = -1.5708
    c: PointOnObject(g11,g2)
    c: PointOnObject(g11,g3)
    c: Tangent(g2,g10) = -1.5708
    c: Tangent(g3,g10) = -1.5708
    c: Equal(g8,g10)
    c: Equal(g10,g4)
    c: Equal(g4,g6)
    c: Radius(g6) = 2
    c: Symmetric(g7,g11,g12)
    c: DistanceX(g-1,g12) = 40
    c: DistanceY(g-1,g12) = 7
    c: DistanceY(g1,g3) = 9
FEATURE [Sketcher::SketchObject] Sketch004
  ArcFitTolerance = 1e-06
  AttachmentSupport = -> [YZ_Plane002]
  ExternalGeometry = -> [Boolean001]
  FullyConstrained = true
  MakeInternals = false
  MapMode = 5
  Placement = pos=(0,0,0) rot=(0.57735,0.57735,0.57735;2.0944rad)
  sketch-geometry (1):
    g0: LineSegment StartX=-84.641 StartY=27 StartZ=0 EndX=-50 EndY=7 EndZ=0
  constraints (3):
    c: Symmetric(g-4,g-4,g0)
    c: Distance(g0) = 40
    c: Angle(g0,g-1) = 0.523599
FEATURE [PartDesign::Pocket] Pocket002
  BaseFeature = -> Boolean001
  Direction = (0,-0.866025,0.5)
  Length = 5
  Length2 = 5
  Profile = -> Sketch003
  ReferenceAxis = -> Sketch004 [Edge1]
  Refine = true
  Suppressed = false
  Type = 1
FEATURE [PartDesign::Body] Body002  label="Top Enclosure Shell - 2"
  AllowCompound = false
  Group = -> [Boolean001,Sketch003,Sketch004,Pocket002]
  Origin = -> Origin002
  Tip = -> Pocket002
FEATURE [PartDesign::SubShapeBinder] Binder010
  BindCopyOnChange = 0
  BindMode = 0
  ClaimChildren = false
  Context = -> Body003 [Binder010.]
  Fuse = false
  MakeFace = true
  OffsetFill = false
  OffsetIntersection = false
  OffsetJoinType = 0
  OffsetOpenResult = false
  PartialLoad = false
  Refine = true
  Relative = true
  Support = -> [Body002]
  _Version = 2
FEATURE [PartDesign::Boolean] Boolean002
  Group = -> [Binder010]
  Refine = true
  Suppressed = false
  Type = 0
  UsePlacement = true
FEATURE [Sketcher::SketchObject] Sketch005
  ArcFitTolerance = 1e-06
  AttachmentSupport = -> [YZ_Plane003]
  FullyConstrained = true
  MakeInternals = false
  MapMode = 5
  Placement = pos=(0,0,0) rot=(0.57735,0.57735,0.57735;2.0944rad)
  expr: Constraints[1] = <<Vars>>.top_enclosure_depth
  expr: Constraints[2] = <<Vars>>.top_enclosure_height / 2 - 10
  sketch-geometry (1):
    g0: LineSegment StartX=-90 StartY=14 StartZ=0 EndX=-40 EndY=14 EndZ=0
  constraints (4):
    c: Horizontal(g0)
    c: DistanceY(g-1,g0) = 14
    c: DistanceX(g0,g-1) = 40
    c: DistanceX(g0,g0) = 50
FEATURE [PartDesign::Body] Body003  label="Top Enclosure Shell Split"
  AllowCompound = false
  Group = -> [Boolean002,Sketch005]
  Origin = -> Origin003
  Tip = -> Boolean002
FEATURE [Part::Extrusion] Extrude
  Base = -> Sketch005
  Dir = (1,0,0)
  DirMode = 2
  FaceMakerClass = Part::FaceMakerBullseye
  FaceMakerMode = 3
  LengthFwd = 280
  LengthRev = 0
  Solid = false
  Symmetric = true
  expr: LengthFwd = <<Vars>>.top_enclosure_width
FEATURE [Part::FeaturePython] Slice  # WARN: FeaturePython — macro-defined, semantics opaque (R4)
  Base = -> Body003
  Mode = 1
  Tolerance = 0
  Tools = -> [Extrude]
FEATURE [Part::FeaturePython] Slice_child0  label="Slice.0"  # WARN: FeaturePython — macro-defined, semantics opaque (R4)
  Base = -> Slice
  FilterType = 1
  Invert = false
  OverrideMaxVal = 0
  WindowFrom = 80
  WindowTo = 100
  items = 0
FEATURE [Part::FeaturePython] Slice_child1  label="Slice.1"  # WARN: FeaturePython — macro-defined, semantics opaque (R4)
  Base = -> Slice
  FilterType = 1
  Invert = false
  OverrideMaxVal = 0
  WindowFrom = 80
  WindowTo = 100
  items = 1
FEATURE [App::DocumentObjectGroup] GrExplode_Slice  label="Exploded Slice"
  Group = -> [Slice_child0,Slice_child1]
FEATURE [PartDesign::SubShapeBinder] Binder011
  BindCopyOnChange = 0
  BindMode = 0
  ClaimChildren = false
  Context = -> Body004 [Binder011.]
  Fuse = false
  MakeFace = true
  OffsetFill = false
  OffsetIntersection = false
  OffsetJoinType = 0
  OffsetOpenResult = false
  PartialLoad = false
  Refine = true
  Relative = true
  Support = -> [Slice_child0]
  _Version = 2
FEATURE [PartDesign::Boolean] Boolean003
  Group = -> [Binder011]
  Refine = true
  Suppressed = false
  Type = 0
  UsePlacement = true
FEATURE [PartDesign::SubShapeBinder] Binder012
  BindCopyOnChange = 0
  BindMode = 0
  ClaimChildren = false
  Context = -> Body005 [Binder012.]
  Fuse = false
  MakeFace = true
  OffsetFill = false
  OffsetIntersection = false
  OffsetJoinType = 0
  OffsetOpenResult = false
  PartialLoad = false
  Refine = true
  Relative = true
  Support = -> [Slice_child1]
  _Version = 2
FEATURE [PartDesign::Boolean] Boolean004
  Group = -> [Binder012]
  Refine = true
  Suppressed = false
  Type = 0
  UsePlacement = true
FEATURE [PartDesign::SubShapeBinder] Binder013
  BindCopyOnChange = 0
  BindMode = 0
  ClaimChildren = false
  Context = -> Body006 [Binder013.]
  Fuse = false
  MakeFace = true
  OffsetFill = false
  OffsetIntersection = false
  OffsetJoinType = 0
  OffsetOpenResult = false
  PartialLoad = false
  Refine = true
  Relative = true
  Support = -> [Slice_child0[Face27]]
  _Version = 2
FEATURE [Sketcher::SketchObject] Sketch006
  ArcFitTolerance = 1e-06
  AttachmentSupport = -> [Binder013]
  ExternalGeometry = -> [Binder013]
  FullyConstrained = true
  MakeInternals = false
  MapMode = 5
  Placement = pos=(0,0,14) rot=(0,0,1;0rad)
  sketch-geometry (2):
    g0: Circle CenterX=-75 CenterY=-62.3412 CenterZ=0 NormalX=0 NormalY=0 NormalZ=1 AngleXU=0 Radius=1.5
    g1: LineSegment [constr] StartX=-75 StartY=-50 StartZ=0 EndX=-75 EndY=-74.6825 EndZ=0
  constraints (6):
    c: Diameter(g0) = 3
    c: PointOnObject(g1,g-5)
    c: PointOnObject(g1,g-6)
    c: Vertical(g1)
    c: Symmetric(g1,g1,g0)
    c: DistanceX(g-3,g1) = 15
FEATURE [PartDesign::SubShapeBinder] Binder014
  BindCopyOnChange = 0
  BindMode = 0
  ClaimChildren = false
  Context = -> Body004 [Binder014.]
  Fuse = false
  MakeFace = true
  OffsetFill = false
  OffsetIntersection = false
  OffsetJoinType = 0
  OffsetOpenResult = false
  PartialLoad = false
  Refine = true
  Relative = true
  Support = -> [Body006[Sketch006.]]
  _Version = 2
FEATURE [PartDesign::Hole] Hole002
  BaseFeature = -> Boolean003
  CustomThreadClearance = 0
  Depth = 6
  DepthType = 0
  Diameter = 4.5
  DrillForDepth = false
  DrillPoint = 1
  DrillPointAngle = 118
  HoleCutCountersinkAngle = 90
  HoleCutCustomValues = false
  HoleCutDepth = 0
  HoleCutDiameter = 6.1
  HoleCutType = 0
  ModelThread = false
  Profile = -> Binder014
  Refine = true
  Suppressed = false
  Tapered = false
  TaperedAngle = 90
  ThreadClass = 0
  ThreadDepth = 6
  ThreadDepthType = 0
  ThreadDirection = 0
  ThreadFit = 0
  ThreadSize = 0
  ThreadType = 0
  Threaded = false
  UseCustomThreadClearance = false
  expr: Diameter = <<Vars>>.nut_inserts_m3
FEATURE [PartDesign::Mirrored] Mirrored004
  BaseFeature = -> Hole002
  MirrorPlane = -> YZ_Plane004
  Originals = -> [Hole002]
  Refine = true
  Suppressed = false
  TransformMode = 0
FEATURE [PartDesign::SubShapeBinder] Binder015
  BindCopyOnChange = 0
  BindMode = 0
  ClaimChildren = false
  Context = -> Body005 [Binder015.]
  Fuse = false
  MakeFace = true
  OffsetFill = false
  OffsetIntersection = false
  OffsetJoinType = 0
  OffsetOpenResult = false
  PartialLoad = false
  Refine = true
  Relative = true
  Support = -> [Body006[Sketch006.]]
  _Version = 2
FEATURE [PartDesign::SubShapeBinder] Binder016
  BindCopyOnChange = 0
  BindMode = 0
  ClaimChildren = false
  Context = -> Body005 [Binder016.]
  Fuse = false
  MakeFace = true
  Offset = 1.5
  OffsetFill = false
  OffsetIntersection = false
  OffsetJoinType = 0
  OffsetOpenResult = false
  PartialLoad = false
  Placement = pos=(0,0,15) rot=(0,0,1;0rad)
  Refine = true
  Relative = true
  Support = -> [Body006[Sketch006.]]
  _Version = 2
FEATURE [PartDesign::Hole] Hole003
  BaseFeature = -> Boolean004
  CustomThreadClearance = 0
  Depth = 25
  DepthType = 0
  Diameter = 3.6
  DrillForDepth = false
  DrillPoint = 1
  DrillPointAngle = 118
  HoleCutCountersinkAngle = 90
  HoleCutCustomValues = false
  HoleCutDepth = 0
  HoleCutDiameter = 6.1
  HoleCutType = 0
  ModelThread = false
  Profile = -> Binder015
  Refine = true
  Reversed = true
  Suppressed = false
  Tapered = false
  TaperedAngle = 90
  ThreadClass = 0
  ThreadDepth = 25
  ThreadDepthType = 0
  ThreadDirection = 0
  ThreadFit = 2
  ThreadSize = 9
  ThreadType = 1
  Threaded = false
  UseCustomThreadClearance = false
FEATURE [PartDesign::Pocket] Pocket003
  BaseFeature = -> Hole003
  Direction = (0,0,-1)
  Length = 10
  Length2 = 5
  Offset = 2
  Profile = -> Binder016
  Refine = true
  Suppressed = false
  Type = 0
FEATURE [PartDesign::Mirrored] Mirrored005
  BaseFeature = -> Pocket003
  MirrorPlane = -> YZ_Plane005
  Originals = -> [Hole003,Pocket003]
  Refine = true
  Suppressed = false
  TransformMode = 0
FEATURE [Sketcher::SketchObject] Sketch007
  ArcFitTolerance = 1e-06
  AttachmentSupport = -> [Binder013]
  ExternalGeometry = -> [Binder013]
  FullyConstrained = true
  MakeInternals = false
  MapMode = 5
  Placement = pos=(0,0,14) rot=(0,0,1;0rad)
  sketch-geometry (2):
    g0: Circle CenterX=-63 CenterY=-62.3412 CenterZ=0 NormalX=0 NormalY=0 NormalZ=1 AngleXU=0 Radius=3
    g1: LineSegment [constr] StartX=-63 StartY=-50 StartZ=0 EndX=-63 EndY=-74.6825 EndZ=0
  constraints (6):
    c: PointOnObject(g1,g-5)
    c: PointOnObject(g1,g-6)
    c: Vertical(g1)
    c: Symmetric(g1,g1,g0)
    c: DistanceX(g1,g-3) = 8
    c: Diameter(g0) = 6
FEATURE [PartDesign::Body] Body006  label="Top Enclosure Shell Hindge Helper"
  AllowCompound = false
  Group = -> [Binder013,Sketch006,Sketch007]
  Origin = -> Origin006
FEATURE [PartDesign::SubShapeBinder] Binder017
  BindCopyOnChange = 0
  BindMode = 0
  ClaimChildren = false
  Context = -> Body004 [Binder017.]
  Fuse = false
  MakeFace = true
  OffsetFill = false
  OffsetIntersection = false
  OffsetJoinType = 0
  OffsetOpenResult = false
  PartialLoad = false
  Refine = true
  Relative = true
  Support = -> [Body006[Sketch007.]]
  _Version = 2
FEATURE [PartDesign::Pocket] Pocket004
  BaseFeature = -> Mirrored004
  Direction = (0,0,-1)
  Length = 4
  Length2 = 5
  Profile = -> Binder017
  Refine = true
  Suppressed = false
  Type = 0
FEATURE [PartDesign::Mirrored] Mirrored006
  BaseFeature = -> Pocket004
  MirrorPlane = -> YZ_Plane004
  Originals = -> [Pocket004]
  Refine = true
  Suppressed = false
  TransformMode = 0
FEATURE [PartDesign::Body] Body004  label="Top Enclosure Shell Part 1"
  AllowCompound = false
  Group = -> [Boolean003,Binder014,Hole002,Mirrored004,Binder017,Pocket004,Mirrored006]
  Origin = -> Origin004
  Tip = -> Mirrored006
FEATURE [PartDesign::SubShapeBinder] Binder018
  BindCopyOnChange = 0
  BindMode = 0
  ClaimChildren = false
  Context = -> Body005 [Binder018.]
  Fuse = false
  MakeFace = true
  OffsetFill = false
  OffsetIntersection = false
  OffsetJoinType = 0
  OffsetOpenResult = false
  PartialLoad = false
  Refine = true
  Relative = true
  Support = -> [Body006[Sketch007.]]
  _Version = 2
FEATURE [PartDesign::Pocket] Pocket005
  BaseFeature = -> Mirrored005
  Direction = (0,0,-1)
  Length = 4
  Length2 = 5
  Profile = -> Binder018
  Refine = true
  Reversed = true
  Suppressed = false
  Type = 0
FEATURE [PartDesign::Mirrored] Mirrored007
  BaseFeature = -> Pocket005
  MirrorPlane = -> YZ_Plane005
  Originals = -> [Pocket005]
  Refine = true
  Suppressed = false
  TransformMode = 0
FEATURE [PartDesign::Body] Body005  label="Top Enclosure Shell Part 2"
  AllowCompound = false
  Group = -> [Boolean004,Binder015,Binder016,Hole003,Pocket003,Mirrored005,Binder018,Pocket005,Mirrored007]
  Origin = -> Origin005
  Tip = -> Mirrored007
FEATURE [App::VarSet] VarSet  label="LocalVars"
  bottom_offset = 2.5
  internal_depth = 6.5
  expr: bottom_offset = <<Vars>>.top_enclosure_back_depth
  expr: internal_depth = <<Vars>>.top_enclosure_internal_depth
FEATURE [PartDesign::SubShapeBinder] Binder019
  BindCopyOnChange = 0
  BindMode = 0
  ClaimChildren = false
  Context = -> Body007 [Binder019.]
  Fuse = false
  MakeFace = true
  OffsetFill = false
  OffsetIntersection = false
  OffsetJoinType = 0
  OffsetOpenResult = false
  PartialLoad = false
  Refine = true
  Relative = true
  Support = -> [Body006[Sketch007.Edge1]]
  _Version = 2
FEATURE [Sketcher::SketchObject] Sketch008
  ArcFitTolerance = 1e-06
  AttachmentSupport = -> [XY_Plane007]
  ExternalGeometry = -> [Binder019]
  FullyConstrained = true
  MakeInternals = false
  MapMode = 5
  expr: Constraints[2] = 6 - <<Vars>>.clearance / 2
  sketch-geometry (1):
    g0: Circle CenterX=0 CenterY=0 CenterZ=0 NormalX=0 NormalY=0 NormalZ=1 AngleXU=0 Radius=2.95
  constraints (3):
    c: Coincident(g0,g-1)
    c: Diameter(g-3) = 6
    c: Diameter(g0) = 5.9
FEATURE [PartDesign::Pad] Pad004
  Direction = (0,0,1)
  Length = 7.6
  Length2 = 10
  Profile = -> Sketch008
  ReferenceAxis = -> Sketch008 [N_Axis]
  Refine = true
  Suppressed = false
  Type = 0
  expr: Length = 8 - 2 * <<Vars>>.clearance
FEATURE [PartDesign::Body] Body007  label="Parts Join Helper"
  AllowCompound = false
  Group = -> [Binder019,Sketch008,Pad004]
  Origin = -> Origin007
  Tip = -> Pad004
